AUTODESK INVENTOR PART (.ipt)
format: ipt  version: 2018 (Build 220112000, 112)  size: 104,690,176 bytes
history: native  units: in
note: dims shown in document units (in); Inventor stores cm internally (conversion verified against a paired STEP export)
features: other x1942, extrude x30
ambient origin geometry x8: Origin, YZ Plane, XZ Plane, XY Plane, X Axis, Y Axis, Z Axis, Center Point
bodies: Solid1 (feature_tree), Solid2 (feature_tree), Solid3 (feature_tree), Solid4 (feature_tree), Solid5 (feature_tree), Solid6 (feature_tree), Solid7 (feature_tree), Solid8 (feature_tree), Solid9 (feature_tree), Solid10 (feature_tree), Solid11 (feature_tree), Solid12 (feature_tree), Solid13 (feature_tree), Solid14 (feature_tree), Solid15 (feature_tree), Solid16 (feature_tree), Solid17 (feature_tree), Solid18 (feature_tree), Solid19 (feature_tree), Solid20 (feature_tree), Solid21 (feature_tree), Solid22 (feature_tree), Solid23 (feature_tree), Solid24 (feature_tree), Solid25 (feature_tree), Solid26 (feature_tree), Solid27 (feature_tree), Solid28 (feature_tree), Solid29 (feature_tree), Solid30 (feature_tree), Solid31 (feature_tree), Solid32 (feature_tree), Solid33 (feature_tree), Solid34 (feature_tree), Solid35 (feature_tree), Solid36 (feature_tree), Solid37 (feature_tree), Solid38 (feature_tree), Solid39 (feature_tree), Solid40 (feature_tree), Solid41 (feature_tree), Solid42 (feature_tree), Solid43 (feature_tree), Solid44 (feature_tree), Solid45 (feature_tree), Solid46 (feature_tree), Solid47 (feature_tree), Solid48 (feature_tree), Solid49 (feature_tree), Solid50 (feature_tree), Solid51 (feature_tree), Solid52 (feature_tree), Solid53 (feature_tree), Solid54 (feature_tree), Solid55 (feature_tree), Solid56 (feature_tree), Solid57 (feature_tree), Solid58 (feature_tree), Solid59 (feature_tree), Solid60 (feature_tree), Solid61 (feature_tree), Solid62 (feature_tree), Solid63 (feature_tree), Solid64 (feature_tree), Solid65 (feature_tree), Solid66 (feature_tree), Solid67 (feature_tree), Solid68 (feature_tree), Solid69 (feature_tree), Solid70 (feature_tree), Solid71 (feature_tree), Solid72 (feature_tree), Solid73 (feature_tree), Solid74 (feature_tree), Solid75 (feature_tree), Solid76 (feature_tree), Solid77 (feature_tree), Solid78 (feature_tree), Solid79 (feature_tree), Solid80 (feature_tree), Solid81 (feature_tree), Solid82 (feature_tree), Solid83 (feature_tree), Solid84 (feature_tree), Solid85 (feature_tree), Solid86 (feature_tree), Solid87 (feature_tree), Solid88 (feature_tree), Solid89 (feature_tree), Solid90 (feature_tree), Solid91 (feature_tree), Solid92 (feature_tree), Solid93 (feature_tree), Solid94 (feature_tree), Solid95 (feature_tree), Solid96 (feature_tree), Solid97 (feature_tree), Solid98 (feature_tree), Solid99 (feature_tree), Solid100 (feature_tree), Solid101 (feature_tree), Solid102 (feature_tree), Solid103 (feature_tree), Solid104 (feature_tree), Solid105 (feature_tree), Solid106 (feature_tree), Solid107 (feature_tree), Solid108 (feature_tree), Solid109 (feature_tree), Solid110 (feature_tree), Solid111 (feature_tree), Solid112 (feature_tree), Solid113 (feature_tree), Solid114 (feature_tree), Solid115 (feature_tree), Solid116 (feature_tree), Solid117 (feature_tree), Solid118 (feature_tree), Solid119 (feature_tree), Solid120 (feature_tree), Solid121 (feature_tree), Solid122 (feature_tree), Solid123 (feature_tree), Solid124 (feature_tree), Solid125 (feature_tree), Solid126 (feature_tree), Solid127 (feature_tree), Solid128 (feature_tree), Solid129 (feature_tree), Solid130 (feature_tree), Solid131 (feature_tree), Solid132 (feature_tree), Solid133 (feature_tree), Solid134 (feature_tree), Solid135 (feature_tree), Solid136 (feature_tree), Solid137 (feature_tree), Solid138 (feature_tree), Solid139 (feature_tree), Solid140 (feature_tree), Solid141 (feature_tree), Solid142 (feature_tree), Solid143 (feature_tree), Solid144 (feature_tree), Solid145 (feature_tree), Solid146 (feature_tree), Solid147 (feature_tree), Solid148 (feature_tree), Solid149 (feature_tree), Solid150 (feature_tree), Solid151 (feature_tree), Solid152 (feature_tree), Solid153 (feature_tree), Solid154 (feature_tree), Solid155 (feature_tree), Solid156 (feature_tree), Solid157 (feature_tree), Solid158 (feature_tree), Solid159 (feature_tree), Solid160 (feature_tree), Solid161 (feature_tree), Solid162 (feature_tree), Solid163 (feature_tree), Solid164 (feature_tree), Solid165 (feature_tree), Solid166 (feature_tree), Solid167 (feature_tree), Solid168 (feature_tree), Solid169 (feature_tree), Solid170 (feature_tree), Solid171 (feature_tree), Solid172 (feature_tree), Solid173 (feature_tree), Solid174 (feature_tree), Solid175 (feature_tree), Solid176 (feature_tree), Solid177 (feature_tree), Solid178 (feature_tree), Solid179 (feature_tree), Solid180 (feature_tree), Solid181 (feature_tree), Solid182 (feature_tree), Solid183 (feature_tree), Solid184 (feature_tree), Solid185 (feature_tree), Solid186 (feature_tree), Solid187 (feature_tree), Solid188 (feature_tree), Solid189 (feature_tree), Solid190 (feature_tree), Solid191 (feature_tree), Solid192 (feature_tree), Solid193 (feature_tree), Solid194 (feature_tree), Solid195 (feature_tree), Solid196 (feature_tree), Solid197 (feature_tree), Solid198 (feature_tree), Solid199 (feature_tree), Solid200 (feature_tree), Solid201 (feature_tree), Solid202 (feature_tree), Solid203 (feature_tree), Solid204 (feature_tree), Solid205 (feature_tree), Solid206 (feature_tree), Solid207 (feature_tree), Solid208 (feature_tree), Solid209 (feature_tree), Solid210 (feature_tree), Solid211 (feature_tree), Solid212 (feature_tree), Solid213 (feature_tree), Solid214 (feature_tree), Solid215 (feature_tree), Solid216 (feature_tree), Solid217 (feature_tree), Solid218 (feature_tree), Solid219 (feature_tree), Solid220 (feature_tree), Solid221 (feature_tree), Solid222 (feature_tree), Solid223 (feature_tree), Solid224 (feature_tree), Solid225 (feature_tree), Solid226 (feature_tree), Solid227 (feature_tree), Solid228 (feature_tree), Solid229 (feature_tree), Solid230 (feature_tree), Solid231 (feature_tree), Solid232 (feature_tree), Solid233 (feature_tree), Solid234 (feature_tree), Solid235 (feature_tree), Solid236 (feature_tree), Solid237 (feature_tree), Solid238 (feature_tree), Solid239 (feature_tree), Solid240 (feature_tree), Solid241 (feature_tree), Solid242 (feature_tree), Solid243 (feature_tree), Solid244 (feature_tree), Solid245 (feature_tree), Solid246 (feature_tree), Solid247 (feature_tree), Solid248 (feature_tree), Solid249 (feature_tree), Solid250 (feature_tree), Solid251 (feature_tree), Solid252 (feature_tree), Solid253 (feature_tree), Solid254 (feature_tree), Solid255 (feature_tree), Solid256 (feature_tree), Solid257 (feature_tree), Solid258 (feature_tree), Solid259 (feature_tree), Solid260 (feature_tree), Solid261 (feature_tree), Solid262 (feature_tree), Solid263 (feature_tree), Solid264 (feature_tree), Solid265 (feature_tree), Solid266 (feature_tree), Solid267 (feature_tree), Solid268 (feature_tree), Solid269 (feature_tree), Solid270 (feature_tree), Solid271 (feature_tree), Solid272 (feature_tree), Solid273 (feature_tree), Solid274 (feature_tree), Solid275 (feature_tree), Solid276 (feature_tree), Solid277 (feature_tree), Solid278 (feature_tree), Solid279 (feature_tree), Solid280 (feature_tree), Solid281 (feature_tree), Solid282 (feature_tree), Solid283 (feature_tree), Solid284 (feature_tree), Solid285 (feature_tree), Solid286 (feature_tree), Solid287 (feature_tree), Solid288 (feature_tree), Solid289 (feature_tree), Solid290 (feature_tree), Solid291 (feature_tree), Solid292 (feature_tree), Solid293 (feature_tree), Solid294 (feature_tree), Solid295 (feature_tree), Solid296 (feature_tree), Solid297 (feature_tree), Solid298 (feature_tree), Solid299 (feature_tree), Solid300 (feature_tree), Solid301 (feature_tree), Solid302 (feature_tree), Solid303 (feature_tree), Solid304 (feature_tree), Solid305 (feature_tree), Solid306 (feature_tree), Solid307 (feature_tree), Solid308 (feature_tree), Solid309 (feature_tree), Solid310 (feature_tree), Solid311 (feature_tree), Solid312 (feature_tree), Solid313 (feature_tree), Solid314 (feature_tree), Solid315 (feature_tree), Solid316 (feature_tree), Solid317 (feature_tree), Solid318 (feature_tree), Solid319 (feature_tree), Solid320 (feature_tree), Solid321 (feature_tree), Solid322 (feature_tree), Solid323 (feature_tree), Solid324 (feature_tree), Solid325 (feature_tree), Solid326 (feature_tree), Solid327 (feature_tree), Solid328 (feature_tree), Solid329 (feature_tree), Solid330 (feature_tree), Solid331 (feature_tree), Solid332 (feature_tree), Solid333 (feature_tree), Solid334 (feature_tree), Solid335 (feature_tree), Solid336 (feature_tree), Solid337 (feature_tree), Solid338 (feature_tree), Solid339 (feature_tree), Solid340 (feature_tree), Solid341 (feature_tree), Solid342 (feature_tree), Solid343 (feature_tree), Solid344 (feature_tree), Solid345 (feature_tree), Solid346 (feature_tree), Solid347 (feature_tree), Solid348 (feature_tree), Solid349 (feature_tree), Solid350 (feature_tree), Solid351 (feature_tree), Solid352 (feature_tree), Solid353 (feature_tree), Solid354 (feature_tree), Solid355 (feature_tree), Solid356 (feature_tree), Solid357 (feature_tree), Solid358 (feature_tree), Solid359 (feature_tree), Solid360 (feature_tree), Solid361 (feature_tree), Solid362 (feature_tree), Solid363 (feature_tree), Solid364 (feature_tree), Solid365 (feature_tree), Solid366 (feature_tree), Solid367 (feature_tree), Solid368 (feature_tree), Solid369 (feature_tree), Solid370 (feature_tree), Solid371 (feature_tree), Solid372 (feature_tree), Solid373 (feature_tree), Solid374 (feature_tree), Solid375 (feature_tree), Solid376 (feature_tree), Solid377 (feature_tree), Solid378 (feature_tree), Solid379 (feature_tree), Solid380 (feature_tree), Solid381 (feature_tree), Solid382 (feature_tree), Solid383 (feature_tree), Solid384 (feature_tree), Solid385 (feature_tree), Solid386 (feature_tree), Solid387 (feature_tree), Solid388 (feature_tree), Solid389 (feature_tree), Solid390 (feature_tree), Solid391 (feature_tree), Solid392 (feature_tree), Solid393 (feature_tree), Solid394 (feature_tree), Solid395 (feature_tree), Solid396 (feature_tree), Solid397 (feature_tree), Solid398 (feature_tree), Solid399 (feature_tree), Solid400 (feature_tree), Solid401 (feature_tree), Solid402 (feature_tree), Solid403 (feature_tree), Solid404 (feature_tree), Solid405 (feature_tree), Solid406 (feature_tree), Solid407 (feature_tree), Solid408 (feature_tree), Solid409 (feature_tree), Solid410 (feature_tree), Solid411 (feature_tree), Solid412 (feature_tree), Solid413 (feature_tree), Solid414 (feature_tree), Solid415 (feature_tree), Solid416 (feature_tree), Solid417 (feature_tree), Solid418 (feature_tree), Solid419 (feature_tree), Solid420 (feature_tree), Solid421 (feature_tree), Solid422 (feature_tree), Solid423 (feature_tree), Solid424 (feature_tree), Solid425 (feature_tree), Solid426 (feature_tree), Solid427 (feature_tree), Solid428 (feature_tree), Solid429 (feature_tree), Solid430 (feature_tree), Solid431 (feature_tree), Solid432 (feature_tree), Solid433 (feature_tree), Solid434 (feature_tree), Solid435 (feature_tree), Solid436 (feature_tree), Solid437 (feature_tree), Solid438 (feature_tree), Solid439 (feature_tree), Solid440 (feature_tree), Solid441 (feature_tree), Solid442 (feature_tree), Solid443 (feature_tree), Solid444 (feature_tree), Solid445 (feature_tree), Solid446 (feature_tree), Solid447 (feature_tree), Solid448 (feature_tree), Solid449 (feature_tree), Solid450 (feature_tree), Solid451 (feature_tree), Solid452 (feature_tree), Solid453 (feature_tree), Solid454 (feature_tree), Solid455 (feature_tree), Solid456 (feature_tree), Solid457 (feature_tree), Solid458 (feature_tree), Solid459 (feature_tree), Solid460 (feature_tree), Solid461 (feature_tree), Solid462 (feature_tree), Solid463 (feature_tree), Solid464 (feature_tree), Solid465 (feature_tree), Solid466 (feature_tree), Solid467 (feature_tree), Solid468 (feature_tree), Solid469 (feature_tree), Solid470 (feature_tree), Solid471 (feature_tree), Solid472 (feature_tree), Solid473 (feature_tree), Solid474 (feature_tree), Solid475 (feature_tree), Solid476 (feature_tree), Solid477 (feature_tree), Solid478 (feature_tree), Solid479 (feature_tree), Solid480 (feature_tree), Solid481 (feature_tree), Solid482 (feature_tree), Solid483 (feature_tree), Solid484 (feature_tree), Solid485 (feature_tree), Solid486 (feature_tree), Solid487 (feature_tree), Solid488 (feature_tree), Solid489 (feature_tree), Solid490 (feature_tree), Solid491 (feature_tree), Solid492 (feature_tree), Solid493 (feature_tree), Solid494 (feature_tree), Solid495 (feature_tree), Solid496 (feature_tree), Solid497 (feature_tree), Solid498 (feature_tree), Solid499 (feature_tree), Solid500 (feature_tree), Solid501 (feature_tree), Solid502 (feature_tree), Solid503 (feature_tree), Solid504 (feature_tree), Solid505 (feature_tree), Solid506 (feature_tree), Solid507 (feature_tree), Solid508 (feature_tree), Solid509 (feature_tree), Solid510 (feature_tree), Solid511 (feature_tree), Solid512 (feature_tree), Solid513 (feature_tree), Solid514 (feature_tree), Solid515 (feature_tree), Solid516 (feature_tree), Solid517 (feature_tree), Solid518 (feature_tree), Solid519 (feature_tree), Solid520 (feature_tree), Solid521 (feature_tree), Solid522 (feature_tree), Solid523 (feature_tree), Solid524 (feature_tree), Solid525 (feature_tree), Solid526 (feature_tree), Solid527 (feature_tree), Solid528 (feature_tree), Solid529 (feature_tree), Solid530 (feature_tree), Solid531 (feature_tree), Solid532 (feature_tree), Solid533 (feature_tree), Solid534 (feature_tree), Solid535 (feature_tree), Solid536 (feature_tree), Solid537 (feature_tree), Solid538 (feature_tree), Solid539 (feature_tree), Solid540 (feature_tree), Solid541 (feature_tree), Solid542 (feature_tree), Solid543 (feature_tree), Solid544 (feature_tree), Solid545 (feature_tree), Solid546 (feature_tree), Solid547 (feature_tree), Solid548 (feature_tree), Solid549 (feature_tree), Solid550 (feature_tree), Solid551 (feature_tree), Solid552 (feature_tree), Solid553 (feature_tree), Solid554 (feature_tree), Solid555 (feature_tree), Solid556 (feature_tree), Solid557 (feature_tree), Solid558 (feature_tree), Solid559 (feature_tree), Solid560 (feature_tree), Solid561 (feature_tree), Solid562 (feature_tree), Solid563 (feature_tree), Solid564 (feature_tree), Solid565 (feature_tree), Solid566 (feature_tree), Solid567 (feature_tree), Solid568 (feature_tree), Solid569 (feature_tree), Solid570 (feature_tree), Solid571 (feature_tree), Solid572 (feature_tree), Solid573 (feature_tree), Solid574 (feature_tree), Solid575 (feature_tree), Solid576 (feature_tree), Solid577 (feature_tree), Solid578 (feature_tree), Solid579 (feature_tree), Solid580 (feature_tree), Solid581 (feature_tree), Solid582 (feature_tree), Solid583 (feature_tree), Solid584 (feature_tree), Solid585 (feature_tree), Solid586 (feature_tree), Solid587 (feature_tree), Solid588 (feature_tree), Solid589 (feature_tree), Solid590 (feature_tree), Solid591 (feature_tree), Solid592 (feature_tree), Solid593 (feature_tree), Solid594 (feature_tree), Solid595 (feature_tree), Solid596 (feature_tree), Solid597 (feature_tree), Solid598 (feature_tree), Solid599 (feature_tree), Solid600 (feature_tree), Solid601 (feature_tree), Solid602 (feature_tree), Solid603 (feature_tree), Solid604 (feature_tree), Solid605 (feature_tree), Solid606 (feature_tree), Solid607 (feature_tree), Solid608 (feature_tree), Solid609 (feature_tree), Solid610 (feature_tree), Solid611 (feature_tree), Solid612 (feature_tree), Solid613 (feature_tree), Solid614 (feature_tree), Solid615 (feature_tree), Solid616 (feature_tree), Solid617 (feature_tree), Solid618 (feature_tree), Solid619 (feature_tree), Solid620 (feature_tree), Solid621 (feature_tree), Solid622 (feature_tree), Solid623 (feature_tree), Solid624 (feature_tree), Solid625 (feature_tree), Solid626 (feature_tree), Solid627 (feature_tree), Solid628 (feature_tree), Solid629 (feature_tree), Solid630 (feature_tree), Solid631 (feature_tree), Solid632 (feature_tree), Solid633 (feature_tree), Solid634 (feature_tree), Solid635 (feature_tree), Solid636 (feature_tree), Solid637 (feature_tree), Solid638 (feature_tree), Solid639 (feature_tree), Solid640 (feature_tree), Solid641 (feature_tree), Solid642 (feature_tree), Solid643 (feature_tree), Solid644 (feature_tree), Solid645 (feature_tree), Solid646 (feature_tree), Solid647 (feature_tree), Solid648 (feature_tree), Solid649 (feature_tree), Solid650 (feature_tree), Solid651 (feature_tree), Solid652 (feature_tree), Solid653 (feature_tree), Solid654 (feature_tree), Solid655 (feature_tree), Solid656 (feature_tree), Solid657 (feature_tree), Solid658 (feature_tree), Solid659 (feature_tree), Solid660 (feature_tree), Solid661 (feature_tree), Solid662 (feature_tree), Solid663 (feature_tree), Solid664 (feature_tree), Solid665 (feature_tree), Solid666 (feature_tree), Solid667 (feature_tree), Solid668 (feature_tree), Solid669 (feature_tree), Solid670 (feature_tree), Solid671 (feature_tree), Solid672 (feature_tree), Solid673 (feature_tree), Solid674 (feature_tree), Solid675 (feature_tree), Solid676 (feature_tree), Solid677 (feature_tree), Solid678 (feature_tree), Solid679 (feature_tree), Solid680 (feature_tree), Solid681 (feature_tree), Solid682 (feature_tree), Solid683 (feature_tree), Solid684 (feature_tree), Solid685 (feature_tree), Solid686 (feature_tree), Solid687 (feature_tree), Solid688 (feature_tree), Solid689 (feature_tree), Solid690 (feature_tree), Solid691 (feature_tree), Solid692 (feature_tree), Solid693 (feature_tree), Solid694 (feature_tree), Solid695 (feature_tree), Solid696 (feature_tree), Solid697 (feature_tree), Solid698 (feature_tree), Solid699 (feature_tree), Solid700 (feature_tree), Solid701 (feature_tree), Solid702 (feature_tree), Solid703 (feature_tree), Solid704 (feature_tree), Solid705 (feature_tree), Solid706 (feature_tree), Solid707 (feature_tree), Solid708 (feature_tree), Solid709 (feature_tree), Solid710 (feature_tree), Solid711 (feature_tree), Solid712 (feature_tree), Solid713 (feature_tree), Solid714 (feature_tree), Solid715 (feature_tree), Solid716 (feature_tree), Solid717 (feature_tree), Solid718 (feature_tree), Solid719 (feature_tree), Solid720 (feature_tree), Solid721 (feature_tree), Solid722 (feature_tree), Solid723 (feature_tree), Solid724 (feature_tree), Solid725 (feature_tree), Solid726 (feature_tree), Solid727 (feature_tree), Solid728 (feature_tree), Solid729 (feature_tree), Solid730 (feature_tree), Solid731 (feature_tree), Solid732 (feature_tree), Solid733 (feature_tree), Solid734 (feature_tree), Solid735 (feature_tree), Solid736 (feature_tree), Solid737 (feature_tree), Solid738 (feature_tree), Solid739 (feature_tree), Solid740 (feature_tree), Solid741 (feature_tree), Solid742 (feature_tree), Solid743 (feature_tree), Solid744 (feature_tree), Solid745 (feature_tree), Solid746 (feature_tree), Solid747 (feature_tree), Solid748 (feature_tree), Solid749 (feature_tree), Solid750 (feature_tree), Solid751 (feature_tree), Solid752 (feature_tree), Solid753 (feature_tree), Solid754 (feature_tree), Solid755 (feature_tree), Solid756 (feature_tree), Solid757 (feature_tree), Solid758 (feature_tree), Solid759 (feature_tree), Solid760 (feature_tree), Solid761 (feature_tree), Solid762 (feature_tree), Solid763 (feature_tree), Solid764 (feature_tree), Solid765 (feature_tree), Solid766 (feature_tree), Solid767 (feature_tree), Solid768 (feature_tree), Solid769 (feature_tree), Solid770 (feature_tree), Solid771 (feature_tree), Solid772 (feature_tree), Solid773 (feature_tree), Solid774 (feature_tree), Solid775 (feature_tree), Solid776 (feature_tree), Solid777 (feature_tree), Solid778 (feature_tree), Solid779 (feature_tree), Solid780 (feature_tree), Solid781 (feature_tree), Solid782 (feature_tree), Solid783 (feature_tree), Solid784 (feature_tree), Solid785 (feature_tree), Solid786 (feature_tree), Solid787 (feature_tree), Solid788 (feature_tree), Solid789 (feature_tree), Solid790 (feature_tree), Solid791 (feature_tree), Solid792 (feature_tree), Solid793 (feature_tree), Solid794 (feature_tree), Solid795 (feature_tree), Solid796 (feature_tree), Solid797 (feature_tree), Solid798 (feature_tree), Solid799 (feature_tree), Solid800 (feature_tree), Solid801 (feature_tree), Solid802 (feature_tree), Solid803 (feature_tree), Solid804 (feature_tree), Solid805 (feature_tree), Solid806 (feature_tree), Solid807 (feature_tree), Solid808 (feature_tree), Solid809 (feature_tree), Solid810 (feature_tree), Solid811 (feature_tree), Solid812 (feature_tree), Solid813 (feature_tree), Solid814 (feature_tree), Solid815 (feature_tree), Solid816 (feature_tree), Solid817 (feature_tree), Solid818 (feature_tree), Solid819 (feature_tree), Solid820 (feature_tree), Solid821 (feature_tree), Solid822 (feature_tree), Solid823 (feature_tree), Solid824 (feature_tree), Solid825 (feature_tree), Solid826 (feature_tree), Solid827 (feature_tree), Solid828 (feature_tree), Solid829 (feature_tree), Solid830 (feature_tree), Solid831 (feature_tree), Solid832 (feature_tree), Solid833 (feature_tree), Solid834 (feature_tree), Solid835 (feature_tree), Solid836 (feature_tree), Solid837 (feature_tree), Solid838 (feature_tree), Solid839 (feature_tree), Solid840 (feature_tree), Solid841 (feature_tree), Solid842 (feature_tree), Solid843 (feature_tree), Solid844 (feature_tree), Solid845 (feature_tree), Solid846 (feature_tree), Solid847 (feature_tree), Solid848 (feature_tree), Solid849 (feature_tree), Solid850 (feature_tree), Solid851 (feature_tree), Solid852 (feature_tree), Solid853 (feature_tree), Solid854 (feature_tree), Solid855 (feature_tree), Solid856 (feature_tree), Solid857 (feature_tree), Solid858 (feature_tree), Solid859 (feature_tree), Solid860 (feature_tree), Solid861 (feature_tree), Solid862 (feature_tree), Solid863 (feature_tree), Solid864 (feature_tree), Solid865 (feature_tree), Solid866 (feature_tree), Solid867 (feature_tree), Solid868 (feature_tree), Solid869 (feature_tree), Solid870 (feature_tree), Solid871 (feature_tree), Solid872 (feature_tree), Solid873 (feature_tree), Solid874 (feature_tree), Solid875 (feature_tree), Solid876 (feature_tree), Solid877 (feature_tree), Solid878 (feature_tree), Solid879 (feature_tree), Solid880 (feature_tree), Solid881 (feature_tree), Solid882 (feature_tree), Solid883 (feature_tree), Solid884 (feature_tree), Solid885 (feature_tree), Solid886 (feature_tree), Solid887 (feature_tree), Solid888 (feature_tree), Solid889 (feature_tree), Solid890 (feature_tree), Solid891 (feature_tree), Solid892 (feature_tree), Solid893 (feature_tree), Solid894 (feature_tree), Solid895 (feature_tree), Solid896 (feature_tree), Solid897 (feature_tree), Solid898 (feature_tree), Solid899 (feature_tree), Solid900 (feature_tree), Solid901 (feature_tree), Solid902 (feature_tree), Solid903 (feature_tree), Solid904 (feature_tree), Solid905 (feature_tree), Solid906 (feature_tree), Solid907 (feature_tree), Solid908 (feature_tree), Solid909 (feature_tree), Solid910 (feature_tree), Solid911 (feature_tree), Solid912 (feature_tree), Solid913 (feature_tree), Solid914 (feature_tree), Solid915 (feature_tree), Solid916 (feature_tree), Solid917 (feature_tree), Solid918 (feature_tree), Solid919 (feature_tree), Solid920 (feature_tree), Solid921 (feature_tree), Solid922 (feature_tree), Solid923 (feature_tree), Solid924 (feature_tree), Solid925 (feature_tree), Solid926 (feature_tree), Solid927 (feature_tree), Solid928 (feature_tree), Solid929 (feature_tree), Solid930 (feature_tree), Solid931 (feature_tree), Solid932 (feature_tree), Solid933 (feature_tree), Solid934 (feature_tree), Solid935 (feature_tree), Solid936 (feature_tree), Solid937 (feature_tree), Solid938 (feature_tree), Solid939 (feature_tree), Solid940 (feature_tree), Solid941 (feature_tree), Solid942 (feature_tree), Solid943 (feature_tree), Solid944 (feature_tree), Solid945 (feature_tree), Solid946 (feature_tree), Solid947 (feature_tree), Solid948 (feature_tree), Solid949 (feature_tree), Solid950 (feature_tree), Solid951 (feature_tree), Solid952 (feature_tree), Solid953 (feature_tree), Solid954 (feature_tree), Solid955 (feature_tree), Solid956 (feature_tree), Solid957 (feature_tree), Solid958 (feature_tree), Solid959 (feature_tree), Solid960 (feature_tree), Solid961 (feature_tree), Solid962 (feature_tree), Solid963 (feature_tree), Solid964 (feature_tree), Solid965 (feature_tree), Solid966 (feature_tree), Solid967 (feature_tree), Solid968 (feature_tree), Solid969 (feature_tree), Solid970 (feature_tree), Solid971 (feature_tree), Solid972 (feature_tree), Solid973 (feature_tree), Solid974 (feature_tree), Solid975 (feature_tree), Solid976 (feature_tree), Solid977 (feature_tree), Solid978 (feature_tree), Solid979 (feature_tree), Solid980 (feature_tree), Solid981 (feature_tree), Solid982 (feature_tree), Solid983 (feature_tree), Solid984 (feature_tree), Solid985 (feature_tree), Solid986 (feature_tree), Solid987 (feature_tree), Solid988 (feature_tree), Solid989 (feature_tree), Solid990 (feature_tree), Solid991 (feature_tree), Solid992 (feature_tree), Solid993 (feature_tree), Solid994 (feature_tree), Solid995 (feature_tree), Solid996 (feature_tree), Solid997 (feature_tree), Solid998 (feature_tree), Solid999 (feature_tree), Solid1000 (feature_tree), Solid1001 (feature_tree), Solid1002 (feature_tree), Solid1003 (feature_tree), Solid1004 (feature_tree), Solid1005 (feature_tree), Solid1006 (feature_tree), Solid1007 (feature_tree), Solid1008 (feature_tree), Solid1009 (feature_tree), Solid1010 (feature_tree), Solid1011 (feature_tree), Solid1012 (feature_tree), Solid1013 (feature_tree), Solid1014 (feature_tree), Solid1015 (feature_tree), Solid1016 (feature_tree), Solid1017 (feature_tree), Solid1018 (feature_tree), Solid1019 (feature_tree), Solid1020 (feature_tree), Solid1021 (feature_tree), Solid1022 (feature_tree), Solid1023 (feature_tree), Solid1024 (feature_tree), Solid1025 (feature_tree), Solid1026 (feature_tree), Solid1027 (feature_tree), Solid1028 (feature_tree), Solid1029 (feature_tree), Solid1030 (feature_tree), Solid1031 (feature_tree), Solid1032 (feature_tree), Solid1033 (feature_tree), Solid1034 (feature_tree), Solid1035 (feature_tree), Solid1036 (feature_tree), Solid1037 (feature_tree), Solid1038 (feature_tree), Solid1039 (feature_tree), Solid1040 (feature_tree), Solid1041 (feature_tree), Solid1042 (feature_tree), Solid1043 (feature_tree), Solid1044 (feature_tree), Solid1045 (feature_tree), Solid1046 (feature_tree), Solid1047 (feature_tree), Solid1048 (feature_tree), Solid1049 (feature_tree), Solid1050 (feature_tree), Solid1051 (feature_tree), Solid1052 (feature_tree), Solid1053 (feature_tree), Solid1054 (feature_tree), Solid1055 (feature_tree), Solid1056 (feature_tree), Solid1057 (feature_tree), Solid1058 (feature_tree), Solid1059 (feature_tree), Solid1060 (feature_tree), Solid1061 (feature_tree), Solid1062 (feature_tree), Solid1063 (feature_tree), Solid1064 (feature_tree), Solid1065 (feature_tree), Solid1066 (feature_tree), Solid1067 (feature_tree), Solid1068 (feature_tree), Solid1069 (feature_tree), Solid1070 (feature_tree), Solid1071 (feature_tree), Solid1072 (feature_tree), Solid1073 (feature_tree), Solid1074 (feature_tree), Solid1075 (feature_tree), Solid1076 (feature_tree), Solid1077 (feature_tree), Solid1078 (feature_tree), Solid1079 (feature_tree), Solid1080 (feature_tree), Solid1081 (feature_tree), Solid1082 (feature_tree), Solid1083 (feature_tree), Solid1084 (feature_tree), Solid1085 (feature_tree), Solid1086 (feature_tree), Solid1087 (feature_tree), Solid1088 (feature_tree), Solid1089 (feature_tree), Solid1090 (feature_tree), Solid1091 (feature_tree), Solid1092 (feature_tree), Solid1093 (feature_tree), Solid1094 (feature_tree), Solid1095 (feature_tree), Solid1096 (feature_tree), Solid1097 (feature_tree), Solid1098 (feature_tree), Solid1099 (feature_tree), Solid1100 (feature_tree), Solid1101 (feature_tree), Solid1102 (feature_tree), Solid1103 (feature_tree), Solid1104 (feature_tree), Solid1105 (feature_tree), Solid1106 (feature_tree), Solid1107 (feature_tree), Solid1108 (feature_tree), Solid1109 (feature_tree), Solid1110 (feature_tree), Solid1111 (feature_tree), Solid1112 (feature_tree), Solid1113 (feature_tree), Solid1114 (feature_tree), Solid1115 (feature_tree), Solid1116 (feature_tree), Solid1117 (feature_tree), Solid1118 (feature_tree), Solid1119 (feature_tree), Solid1120 (feature_tree), Solid1121 (feature_tree), Solid1122 (feature_tree), Solid1123 (feature_tree), Solid1124 (feature_tree), Solid1125 (feature_tree), Solid1126 (feature_tree), Solid1127 (feature_tree), Solid1128 (feature_tree), Solid1129 (feature_tree), Solid1130 (feature_tree), Solid1131 (feature_tree), Solid1132 (feature_tree), Solid1133 (feature_tree), Solid1134 (feature_tree), Solid1135 (feature_tree), Solid1136 (feature_tree), Solid1137 (feature_tree), Solid1138 (feature_tree), Solid1139 (feature_tree), Solid1140 (feature_tree), Solid1141 (feature_tree), Solid1142 (feature_tree), Solid1143 (feature_tree), Solid1144 (feature_tree), Solid1145 (feature_tree), Solid1146 (feature_tree), Solid1147 (feature_tree), Solid1148 (feature_tree), Solid1149 (feature_tree), Solid1150 (feature_tree), Solid1151 (feature_tree), Solid1152 (feature_tree), Solid1153 (feature_tree), Solid1154 (feature_tree), Solid1155 (feature_tree), Solid1156 (feature_tree), Solid1157 (feature_tree), Solid1158 (feature_tree), Solid1159 (feature_tree), Solid1160 (feature_tree), Solid1161 (feature_tree), Solid1162 (feature_tree), Solid1163 (feature_tree), Solid1164 (feature_tree), Solid1165 (feature_tree), Solid1166 (feature_tree), Solid1167 (feature_tree), Solid1168 (feature_tree), Solid1169 (feature_tree), Solid1170 (feature_tree), Solid1171 (feature_tree), Solid1172 (feature_tree), Solid1173 (feature_tree), Solid1174 (feature_tree), Solid1175 (feature_tree), Solid1176 (feature_tree), Solid1177 (feature_tree), Solid1178 (feature_tree), Solid1179 (feature_tree), Solid1180 (feature_tree), Solid1181 (feature_tree), Solid1182 (feature_tree), Solid1183 (feature_tree), Solid1184 (feature_tree), Solid1185 (feature_tree), Solid1186 (feature_tree), Solid1187 (feature_tree), Solid1188 (feature_tree), Solid1189 (feature_tree), Solid1190 (feature_tree), Solid1191 (feature_tree), Solid1192 (feature_tree), Solid1193 (feature_tree), Solid1194 (feature_tree), Solid1195 (feature_tree), Solid1196 (feature_tree), Solid1197 (feature_tree), Solid1198 (feature_tree), Solid1199 (feature_tree), Solid1200 (feature_tree), Solid1201 (feature_tree), Solid1202 (feature_tree), Solid1203 (feature_tree), Solid1204 (feature_tree), Solid1205 (feature_tree), Solid1206 (feature_tree), Solid1207 (feature_tree), Solid1208 (feature_tree), Solid1209 (feature_tree), Solid1210 (feature_tree), Solid1211 (feature_tree), Solid1212 (feature_tree), Solid1213 (feature_tree), Solid1214 (feature_tree), Solid1215 (feature_tree), Solid1216 (feature_tree), Solid1217 (feature_tree), Solid1218 (feature_tree), Solid1219 (feature_tree), Solid1220 (feature_tree), Solid1221 (feature_tree), Solid1222 (feature_tree), Solid1223 (feature_tree), Solid1224 (feature_tree), Solid1225 (feature_tree), Solid1226 (feature_tree), Solid1227 (feature_tree), Solid1228 (feature_tree), Solid1229 (feature_tree), Solid1230 (feature_tree), Solid1231 (feature_tree), Solid1232 (feature_tree), Solid1233 (feature_tree), Solid1234 (feature_tree), Solid1235 (feature_tree), Solid1236 (feature_tree), Solid1237 (feature_tree), Solid1238 (feature_tree), Solid1239 (feature_tree), Solid1240 (feature_tree), Solid1241 (feature_tree), Solid1242 (feature_tree), Solid1243 (feature_tree), Solid1244 (feature_tree), Solid1245 (feature_tree), Solid1246 (feature_tree), Solid1247 (feature_tree), Solid1248 (feature_tree), Solid1249 (feature_tree), Solid1250 (feature_tree), Solid1251 (feature_tree), Solid1252 (feature_tree), Solid1253 (feature_tree), Solid1254 (feature_tree), Solid1255 (feature_tree), Solid1256 (feature_tree), Solid1257 (feature_tree), Solid1258 (feature_tree), Solid1259 (feature_tree), Solid1260 (feature_tree), Solid1261 (feature_tree), Solid1262 (feature_tree), Solid1263 (feature_tree), Solid1264 (feature_tree), Solid1265 (feature_tree), Solid1266 (feature_tree), Solid1267 (feature_tree), Solid1268 (feature_tree), Solid1269 (feature_tree), Solid1270 (feature_tree), Solid1271 (feature_tree), Solid1272 (feature_tree), Solid1273 (feature_tree), Solid1274 (feature_tree), Solid1275 (feature_tree), Solid1276 (feature_tree), Solid1277 (feature_tree), Solid1278 (feature_tree), Solid1279 (feature_tree), Solid1280 (feature_tree), Solid1281 (feature_tree), Solid1282 (feature_tree), Solid1283 (feature_tree), Solid1284 (feature_tree), Solid1285 (feature_tree), Solid1286 (feature_tree), Solid1287 (feature_tree), Solid1288 (feature_tree), Solid1289 (feature_tree), Solid1290 (feature_tree), Solid1291 (feature_tree), Solid1292 (feature_tree), Solid1293 (feature_tree), Solid1294 (feature_tree), Solid1295 (feature_tree), Solid1296 (feature_tree), Solid1297 (feature_tree), Solid1298 (feature_tree), Solid1299 (feature_tree), Solid1300 (feature_tree), Solid1301 (feature_tree), Solid1302 (feature_tree), Solid1303 (feature_tree), Solid1304 (feature_tree), Solid1305 (feature_tree), Solid1306 (feature_tree), Solid1307 (feature_tree), Solid1308 (feature_tree), Solid1309 (feature_tree), Solid1310 (feature_tree), Solid1311 (feature_tree), Solid1312 (feature_tree), Solid1313 (feature_tree), Solid1314 (feature_tree), Solid1315 (feature_tree), Solid1316 (feature_tree), Solid1317 (feature_tree), Solid1318 (feature_tree), Solid1319 (feature_tree), Solid1320 (feature_tree), Solid1321 (feature_tree), Solid1322 (feature_tree), Solid1323 (feature_tree), Solid1324 (feature_tree), Solid1325 (feature_tree), Solid1326 (feature_tree), Solid1327 (feature_tree), Solid1328 (feature_tree), Solid1329 (feature_tree), Solid1330 (feature_tree), Solid1331 (feature_tree), Solid1332 (feature_tree), Solid1333 (feature_tree), Solid1334 (feature_tree), Solid1335 (feature_tree), Solid1336 (feature_tree), Solid1337 (feature_tree), Solid1338 (feature_tree), Solid1339 (feature_tree), Solid1340 (feature_tree), Solid1341 (feature_tree), Solid1342 (feature_tree), Solid1343 (feature_tree), Solid1344 (feature_tree), Solid1345 (feature_tree), Solid1346 (feature_tree), Solid1347 (feature_tree), Solid1348 (feature_tree), Solid1349 (feature_tree), Solid1350 (feature_tree), Solid1351 (feature_tree), Solid1352 (feature_tree), Solid1353 (feature_tree), Solid1354 (feature_tree), Solid1355 (feature_tree), Solid1356 (feature_tree), Solid1357 (feature_tree), Solid1358 (feature_tree), Solid1359 (feature_tree), Solid1360 (feature_tree), Solid1361 (feature_tree), Solid1362 (feature_tree), Solid1363 (feature_tree), Solid1364 (feature_tree), Solid1365 (feature_tree), Solid1366 (feature_tree), Solid1367 (feature_tree), Solid1368 (feature_tree), Solid1369 (feature_tree), Solid1370 (feature_tree), Solid1371 (feature_tree), Solid1372 (feature_tree), Solid1373 (feature_tree), Solid1374 (feature_tree), Solid1375 (feature_tree), Solid1376 (feature_tree), Solid1377 (feature_tree), Solid1378 (feature_tree), Solid1379 (feature_tree), Solid1380 (feature_tree), Solid1381 (feature_tree), Solid1382 (feature_tree), Solid1383 (feature_tree), Solid1384 (feature_tree), Solid1385 (feature_tree), Solid1386 (feature_tree), Solid1387 (feature_tree), Solid1388 (feature_tree), Solid1389 (feature_tree), Solid1390 (feature_tree), Solid1391 (feature_tree), Solid1392 (feature_tree), Solid1393 (feature_tree), Solid1394 (feature_tree), Solid1395 (feature_tree), Solid1396 (feature_tree), Solid1397 (feature_tree), Solid1398 (feature_tree), Solid1399 (feature_tree), Solid1400 (feature_tree), Solid1401 (feature_tree), Solid1402 (feature_tree), Solid1403 (feature_tree), Solid1404 (feature_tree), Solid1405 (feature_tree), Solid1406 (feature_tree), Solid1407 (feature_tree), Solid1408 (feature_tree), Solid1409 (feature_tree), Solid1410 (feature_tree), Solid1411 (feature_tree), Solid1412 (feature_tree), Solid1413 (feature_tree), Solid1414 (feature_tree), Solid1415 (feature_tree), Solid1416 (feature_tree), Solid1417 (feature_tree), Solid1418 (feature_tree), Solid1419 (feature_tree), Solid1420 (feature_tree), Solid1421 (feature_tree), Solid1422 (feature_tree), Solid1423 (feature_tree), Solid1424 (feature_tree), Solid1425 (feature_tree), Solid1426 (feature_tree), Solid1427 (feature_tree), Solid1428 (feature_tree), Solid1429 (feature_tree), Solid1430 (feature_tree), Solid1431 (feature_tree), Solid1432 (feature_tree), Solid1433 (feature_tree), Solid1434 (feature_tree), Solid1435 (feature_tree), Solid1436 (feature_tree), Solid1437 (feature_tree), Solid1438 (feature_tree), Solid1439 (feature_tree), Solid1440 (feature_tree), Solid1441 (feature_tree), Solid1442 (feature_tree), Solid1443 (feature_tree), Solid1444 (feature_tree), Solid1445 (feature_tree), Solid1446 (feature_tree), Solid1447 (feature_tree), Solid1448 (feature_tree), Solid1449 (feature_tree), Solid1450 (feature_tree), Solid1451 (feature_tree), Solid1452 (feature_tree), Solid1453 (feature_tree), Solid1454 (feature_tree), Solid1455 (feature_tree), Solid1456 (feature_tree), Solid1457 (feature_tree), Solid1458 (feature_tree), Solid1459 (feature_tree), Solid1460 (feature_tree), Solid1461 (feature_tree), Solid1462 (feature_tree), Solid1463 (feature_tree), Solid1464 (feature_tree), Solid1465 (feature_tree), Solid1466 (feature_tree), Solid1467 (feature_tree), Solid1468 (feature_tree), Solid1469 (feature_tree), Solid1470 (feature_tree), Solid1471 (feature_tree), Solid1472 (feature_tree), Solid1473 (feature_tree), Solid1474 (feature_tree), Solid1475 (feature_tree), Solid1476 (feature_tree), Solid1477 (feature_tree), Solid1478 (feature_tree), Solid1479 (feature_tree), Solid1480 (feature_tree), Solid1481 (feature_tree), Solid1482 (feature_tree), Solid1483 (feature_tree), Solid1484 (feature_tree), Solid1485 (feature_tree), Solid1486 (feature_tree), Solid1487 (feature_tree), Solid1488 (feature_tree), Solid1489 (feature_tree), Solid1490 (feature_tree), Solid1491 (feature_tree), Solid1492 (feature_tree), Solid1493 (feature_tree), Solid1494 (feature_tree), Solid1495 (feature_tree), Solid1496 (feature_tree), Solid1497 (feature_tree), Solid1498 (feature_tree), Solid1499 (feature_tree), Solid1500 (feature_tree), Solid1501 (feature_tree), Solid1502 (feature_tree), Solid1503 (feature_tree), Solid1504 (feature_tree), Solid1505 (feature_tree), Solid1506 (feature_tree), Solid1507 (feature_tree), Solid1508 (feature_tree), Solid1509 (feature_tree), Solid1510 (feature_tree), Solid1511 (feature_tree), Solid1512 (feature_tree), Solid1513 (feature_tree), Solid1514 (feature_tree), Solid1515 (feature_tree), Solid1516 (feature_tree), Solid1517 (feature_tree), Solid1518 (feature_tree), Solid1519 (feature_tree), Solid1520 (feature_tree), Solid1521 (feature_tree), Solid1522 (feature_tree), Solid1523 (feature_tree), Solid1524 (feature_tree), Solid1525 (feature_tree), Solid1526 (feature_tree), Solid1527 (feature_tree), Solid1528 (feature_tree), Solid1529 (feature_tree), Solid1530 (feature_tree), Solid1531 (feature_tree), Solid1532 (feature_tree), Solid1533 (feature_tree), Solid1534 (feature_tree), Solid1535 (feature_tree), Solid1536 (feature_tree), Solid1537 (feature_tree), Solid1538 (feature_tree), Solid1539 (feature_tree), Solid1540 (feature_tree), Solid1541 (feature_tree), Solid1542 (feature_tree), Solid1543 (feature_tree), Solid1544 (feature_tree), Solid1545 (feature_tree), Solid1546 (feature_tree), Solid1547 (feature_tree), Solid1548 (feature_tree), Solid1549 (feature_tree), Solid1550 (feature_tree), Solid1551 (feature_tree), Solid1552 (feature_tree), Solid1553 (feature_tree), Solid1554 (feature_tree), Solid1555 (feature_tree), Solid1556 (feature_tree), Solid1557 (feature_tree), Solid1558 (feature_tree), Solid1559 (feature_tree), Solid1560 (feature_tree), Solid1561 (feature_tree), Solid1562 (feature_tree), Solid1563 (feature_tree), Solid1564 (feature_tree), Solid1565 (feature_tree), Solid1566 (feature_tree), Solid1567 (feature_tree), Solid1568 (feature_tree), Solid1569 (feature_tree), Solid1570 (feature_tree), Solid1571 (feature_tree), Solid1572 (feature_tree), Solid1573 (feature_tree), Solid1574 (feature_tree), Solid1575 (feature_tree), Solid1576 (feature_tree), Solid1577 (feature_tree), Solid1578 (feature_tree), Solid1579 (feature_tree), Solid1580 (feature_tree), Solid1581 (feature_tree), Solid1582 (feature_tree), Solid1583 (feature_tree), Solid1584 (feature_tree), Solid1585 (feature_tree), Solid1586 (feature_tree), Solid1587 (feature_tree), Solid1588 (feature_tree), Solid1589 (feature_tree), Solid1590 (feature_tree), Solid1591 (feature_tree), Solid1592 (feature_tree), Solid1593 (feature_tree), Solid1594 (feature_tree), Solid1595 (feature_tree), Solid1596 (feature_tree), Solid1597 (feature_tree), Solid1598 (feature_tree), Solid1599 (feature_tree), Solid1600 (feature_tree), Solid1601 (feature_tree), Solid1602 (feature_tree), Solid1603 (feature_tree), Solid1604 (feature_tree), Solid1605 (feature_tree), Solid1606 (feature_tree), Solid1607 (feature_tree), Solid1608 (feature_tree), Solid1609 (feature_tree), Solid1610 (feature_tree), Solid1611 (feature_tree), Solid1612 (feature_tree), Solid1613 (feature_tree), Solid1614 (feature_tree), Solid1615 (feature_tree), Solid1616 (feature_tree), Solid1617 (feature_tree), Solid1618 (feature_tree), Solid1619 (feature_tree), Solid1620 (feature_tree), Solid1621 (feature_tree), Solid1622 (feature_tree), Solid1623 (feature_tree), Solid1624 (feature_tree), Solid1625 (feature_tree), Solid1626 (feature_tree), Solid1627 (feature_tree), Solid1628 (feature_tree), Solid1629 (feature_tree), Solid1630 (feature_tree), Solid1631 (feature_tree), Solid1632 (feature_tree), Solid1633 (feature_tree), Solid1634 (feature_tree), Solid1635 (feature_tree), Solid1636 (feature_tree), Solid1637 (feature_tree), Solid1638 (feature_tree), Solid1639 (feature_tree), Solid1640 (feature_tree), Solid1641 (feature_tree), Solid1642 (feature_tree), Solid1643 (feature_tree), Solid1644 (feature_tree), Solid1645 (feature_tree), Solid1646 (feature_tree), Solid1647 (feature_tree), Solid1648 (feature_tree), Solid1649 (feature_tree), Solid1650 (feature_tree), Solid1651 (feature_tree), Solid1652 (feature_tree), Solid1653 (feature_tree), Solid1654 (feature_tree), Solid1655 (feature_tree), Solid1656 (feature_tree), Solid1657 (feature_tree), Solid1658 (feature_tree), Solid1659 (feature_tree), Solid1660 (feature_tree), Solid1661 (feature_tree), Solid1662 (feature_tree), Solid1663 (feature_tree), Solid1664 (feature_tree), Solid1665 (feature_tree), Solid1666 (feature_tree), Solid1667 (feature_tree), Solid1668 (feature_tree), Solid1669 (feature_tree), Solid1670 (feature_tree), Solid1671 (feature_tree), Solid1672 (feature_tree), Solid1673 (feature_tree), Solid1674 (feature_tree), Solid1675 (feature_tree), Solid1676 (feature_tree), Solid1677 (feature_tree), Solid1678 (feature_tree), Solid1679 (feature_tree), Solid1680 (feature_tree), Solid1681 (feature_tree), Solid1682 (feature_tree), Solid1683 (feature_tree), Solid1684 (feature_tree), Solid1685 (feature_tree), Solid1686 (feature_tree), Solid1687 (feature_tree), Solid1688 (feature_tree), Solid1689 (feature_tree), Solid1690 (feature_tree), Solid1691 (feature_tree), Solid1692 (feature_tree), Solid1693 (feature_tree), Solid1694 (feature_tree), Solid1695 (feature_tree), Solid1696 (feature_tree), Solid1697 (feature_tree), Solid1698 (feature_tree), Solid1699 (feature_tree), Solid1700 (feature_tree), Solid1701 (feature_tree), Solid1702 (feature_tree), Solid1703 (feature_tree), Solid1704 (feature_tree), Solid1705 (feature_tree), Solid1706 (feature_tree), Solid1707 (feature_tree), Solid1708 (feature_tree), Solid1709 (feature_tree), Solid1710 (feature_tree), Solid1711 (feature_tree), Solid1712 (feature_tree), Solid1713 (feature_tree), Solid1714 (feature_tree), Solid1715 (feature_tree), Solid1716 (feature_tree), Solid1717 (feature_tree), Solid1718 (feature_tree), Solid1719 (feature_tree), Solid1720 (feature_tree), Solid1721 (feature_tree), Solid1722 (feature_tree), Solid1723 (feature_tree), Solid1724 (feature_tree), Solid1725 (feature_tree), Solid1726 (feature_tree), Solid1727 (feature_tree), Solid1728 (feature_tree), Solid1729 (feature_tree), Solid1730 (feature_tree), Solid1731 (feature_tree), Solid1732 (feature_tree), Solid1733 (feature_tree), Solid1734 (feature_tree), Solid1735 (feature_tree), Solid1736 (feature_tree), Solid1737 (feature_tree), Solid1738 (feature_tree), Solid1739 (feature_tree), Solid1740 (feature_tree), Solid1741 (feature_tree), Solid1742 (feature_tree), Solid1743 (feature_tree), Solid1744 (feature_tree), Solid1745 (feature_tree), Solid1746 (feature_tree), Solid1747 (feature_tree), Solid1748 (feature_tree), Solid1749 (feature_tree), Solid1750 (feature_tree), Solid1751 (feature_tree), Solid1752 (feature_tree), Solid1753 (feature_tree), Solid1754 (feature_tree), Solid1755 (feature_tree), Solid1756 (feature_tree), Solid1757 (feature_tree), Solid1758 (feature_tree), Solid1759 (feature_tree), Solid1760 (feature_tree), Solid1761 (feature_tree), Solid1762 (feature_tree), Solid1763 (feature_tree), Solid1764 (feature_tree), Solid1765 (feature_tree), Solid1766 (feature_tree), Solid1767 (feature_tree), Solid1768 (feature_tree), Solid1769 (feature_tree), Solid1770 (feature_tree), Solid1771 (feature_tree), Solid1772 (feature_tree), Solid1773 (feature_tree), Solid1774 (feature_tree), Solid1775 (feature_tree), Solid1776 (feature_tree), Solid1777 (feature_tree), Solid1778 (feature_tree), Solid1779 (feature_tree), Solid1780 (feature_tree), Solid1781 (feature_tree), Solid1782 (feature_tree), Solid1783 (feature_tree), Solid1784 (feature_tree), Solid1785 (feature_tree), Solid1786 (feature_tree), Solid1787 (feature_tree), Solid1788 (feature_tree), Solid1789 (feature_tree), Solid1790 (feature_tree), Solid1791 (feature_tree), Solid1792 (feature_tree), Solid1793 (feature_tree), Solid1794 (feature_tree), Solid1795 (feature_tree), Solid1796 (feature_tree), Solid1797 (feature_tree), Solid1798 (feature_tree), Solid1799 (feature_tree), Solid1800 (feature_tree), Solid1801 (feature_tree), Solid1802 (feature_tree), Solid1803 (feature_tree), Solid1804 (feature_tree), Solid1805 (feature_tree), Solid1806 (feature_tree), Solid1807 (feature_tree), Solid1808 (feature_tree), Solid1809 (feature_tree), Solid1810 (feature_tree), Solid1811 (feature_tree), Solid1812 (feature_tree), Solid1813 (feature_tree), Solid1814 (feature_tree), Solid1815 (feature_tree), Solid1816 (feature_tree), Solid1817 (feature_tree), Solid1818 (feature_tree), Solid1819 (feature_tree), Solid1820 (feature_tree), Solid1821 (feature_tree), Solid1822 (feature_tree), Solid1823 (feature_tree), Solid1824 (feature_tree), Solid1825 (feature_tree), Solid1826 (feature_tree), Solid1827 (feature_tree), Solid1828 (feature_tree), Solid1829 (feature_tree), Solid1830 (feature_tree), Solid1831 (feature_tree), Solid1832 (feature_tree), Solid1833 (feature_tree), Solid1834 (feature_tree), Solid1835 (feature_tree), Solid1836 (feature_tree), Solid1837 (feature_tree), Solid1838 (feature_tree), Solid1839 (feature_tree), Solid1840 (feature_tree), Solid1841 (feature_tree), Solid1842 (feature_tree), Solid1843 (feature_tree), Solid1844 (feature_tree), Solid1845 (feature_tree), Solid1846 (feature_tree), Solid1847 (feature_tree), Solid1848 (feature_tree), Solid1849 (feature_tree), Solid1850 (feature_tree), Solid1851 (feature_tree), Solid1852 (feature_tree), Solid1853 (feature_tree), Solid1854 (feature_tree), Solid1855 (feature_tree), Solid1856 (feature_tree), Solid1857 (feature_tree), Solid1858 (feature_tree), Solid1859 (feature_tree), Solid1860 (feature_tree), Solid1861 (feature_tree), Solid1862 (feature_tree), Solid1863 (feature_tree), Solid1864 (feature_tree), Solid1865 (feature_tree), Solid1866 (feature_tree), Solid1867 (feature_tree), Solid1868 (feature_tree), Solid1869 (feature_tree), Solid1870 (feature_tree), Solid1871 (feature_tree), Solid1872 (feature_tree), Solid1873 (feature_tree), Solid1874 (feature_tree), Solid1875 (feature_tree), Solid1876 (feature_tree), Solid1877 (feature_tree), Solid1878 (feature_tree), Solid1879 (feature_tree), Solid1880 (feature_tree), Solid1881 (feature_tree), Solid1882 (feature_tree), Solid1883 (feature_tree), Solid1884 (feature_tree), Solid1885 (feature_tree), Solid1886 (feature_tree), Solid1887 (feature_tree), Solid1888 (feature_tree), Solid1889 (feature_tree), Solid1890 (feature_tree), Solid1891 (feature_tree), Solid1892 (feature_tree), Solid1893 (feature_tree), Solid1894 (feature_tree), Solid1895 (feature_tree), Solid1896 (feature_tree), Solid1897 (feature_tree), Solid1898 (feature_tree), Solid1899 (feature_tree), Solid1900 (feature_tree), Solid1901 (feature_tree), Solid1902 (feature_tree), Solid1903 (feature_tree), Solid1904 (feature_tree), Solid1905 (feature_tree), Solid1906 (feature_tree), Solid1907 (feature_tree), Solid1908 (feature_tree), Solid1909 (feature_tree), Solid1910 (feature_tree), Solid1911 (feature_tree), Solid1912 (feature_tree), Solid1913 (feature_tree), Solid1914 (feature_tree), Solid1915 (feature_tree), Solid1916 (feature_tree), Solid1917 (feature_tree), Solid1918 (feature_tree), Solid1919 (feature_tree), Solid1920 (feature_tree), Solid1921 (feature_tree), Solid1922 (feature_tree), Solid1923 (feature_tree), Solid1924 (feature_tree), Solid1925 (feature_tree), Solid1926 (feature_tree), Solid1927 (feature_tree), Solid1928 (feature_tree), Solid1929 (feature_tree), Solid1930 (feature_tree), Solid1931 (feature_tree), Solid1932 (feature_tree), Solid1933 (feature_tree), Solid1934 (feature_tree), Solid1935 (feature_tree), Solid1936 (feature_tree), Solid1937 (feature_tree), Solid1938 (feature_tree), Solid1939 (feature_tree), Solid1940 (feature_tree), Solid1941 (feature_tree), Solid1942 (feature_tree), Solid1943 (feature_tree), Solid1944 (feature_tree), Solid1945 (feature_tree), Solid1946 (feature_tree), Solid1947 (feature_tree), Solid1948 (feature_tree), Solid1949 (feature_tree), Solid1950 (feature_tree), Solid1951 (feature_tree), Solid1952 (feature_tree), Solid1953 (feature_tree), Solid1954 (feature_tree), Solid1955 (feature_tree), Solid1956 (feature_tree), Solid1957 (feature_tree), Solid1958 (feature_tree), Solid1959 (feature_tree), Solid1960 (feature_tree), Solid1961 (feature_tree), Solid1962 (feature_tree), Solid1963 (feature_tree), Solid1964 (feature_tree), Solid1965 (feature_tree), Solid1966 (feature_tree), Solid1967 (feature_tree), Solid1968 (feature_tree), Solid1969 (feature_tree), Solid1970 (feature_tree)
feature tree (1972):
  other  "Board_1:1"
  other  "User_Library-0402(1005M)_Cap_2:1"
  other  "User_Library-0402(1005M)_Cap_2:2"
  other  "User_Library-0402(1005M)_Cap_2:3"
  other  "RES-0201(0603mm)_4:1"
  other  "RES-0201(0603mm)_4:2"
  other  "RES-0201(0603mm)_4:3"
  other  "RES-0201(0603mm)_4:4"
  other  "User_Library-0201(0603M)_Cap_6:1"
  other  "User_Library-0201(0603M)_Cap_6:2"
  other  "User_Library-0201(0603M)_Cap_6:3"
  other  "User_Library-0201(0603M)_Cap_8:1"
  other  "User_Library-0201(0603M)_Cap_8:2"
  other  "User_Library-0201(0603M)_Cap_8:3"
  other  "RES-0201(0603mm)_10:1"
  other  "RES-0201(0603mm)_10:2"
  other  "RES-0201(0603mm)_10:3"
  other  "RES-0201(0603mm)_10:4"
  other  "RES-0201(0603mm)_12:1"
  other  "RES-0201(0603mm)_12:2"
  other  "RES-0201(0603mm)_12:3"
  other  "RES-0201(0603mm)_12:4"
  other  "RES-0201(0603mm)_14:1"
  other  "RES-0201(0603mm)_14:2"
  other  "RES-0201(0603mm)_14:3"
  other  "RES-0201(0603mm)_14:4"
  other  "RES-0201(0603mm)_16:1"
  other  "RES-0201(0603mm)_16:2"
  other  "RES-0201(0603mm)_16:3"
  other  "RES-0201(0603mm)_16:4"
  extrude  "Extruded_18:1"  [1 undecoded]
  other  "Cylinder_21:1"
  extrude  "Extruded_23:1"  [1 undecoded]
  other  "RES-0201(0603mm)_26:1"
  other  "RES-0201(0603mm)_26:2"
  other  "RES-0201(0603mm)_26:3"
  other  "RES-0201(0603mm)_26:4"
  other  "RES-0201(0603mm)_28:1"
  other  "RES-0201(0603mm)_28:2"
  other  "RES-0201(0603mm)_28:3"
  other  "RES-0201(0603mm)_28:4"
  other  "RES-0201(0603mm)_30:1"
  other  "RES-0201(0603mm)_30:2"
  other  "RES-0201(0603mm)_30:3"
  other  "RES-0201(0603mm)_30:4"
  other  "RES-0201(0603mm)_32:1"
  other  "RES-0201(0603mm)_32:2"
  other  "RES-0201(0603mm)_32:3"
  other  "RES-0201(0603mm)_32:4"
  other  "RES-0201(0603mm)_34:1"
  other  "RES-0201(0603mm)_34:2"
  other  "RES-0201(0603mm)_34:3"
  other  "RES-0201(0603mm)_34:4"
  other  "RES-0201(0603mm)_36:1"
  other  "RES-0201(0603mm)_36:2"
  other  "RES-0201(0603mm)_36:3"
  other  "RES-0201(0603mm)_36:4"
  other  "RES-0201(0603mm)_38:1"
  other  "RES-0201(0603mm)_38:2"
  other  "RES-0201(0603mm)_38:3"
  other  "RES-0201(0603mm)_38:4"
  other  "RES-0201(0603mm)_40:1"
  other  "RES-0201(0603mm)_40:2"
  other  "RES-0201(0603mm)_40:3"
  other  "RES-0201(0603mm)_40:4"
  other  "RES-0201(0603mm)_42:1"
  other  "RES-0201(0603mm)_42:2"
  other  "RES-0201(0603mm)_42:3"
  other  "RES-0201(0603mm)_42:4"
  other  "RES-0201(0603mm)_44:1"
  other  "RES-0201(0603mm)_44:2"
  other  "RES-0201(0603mm)_44:3"
  other  "RES-0201(0603mm)_44:4"
  other  "RES-0201(0603mm)_46:1"
  other  "RES-0201(0603mm)_46:2"
  other  "RES-0201(0603mm)_46:3"
  other  "RES-0201(0603mm)_46:4"
  other  "RES-0201(0603mm)_48:1"
  other  "RES-0201(0603mm)_48:2"
  other  "RES-0201(0603mm)_48:3"
  other  "RES-0201(0603mm)_48:4"
  other  "RES-0201(0603mm)_50:1"
  other  "RES-0201(0603mm)_50:2"
  other  "RES-0201(0603mm)_50:3"
  other  "RES-0201(0603mm)_50:4"
  other  "RES-0201(0603mm)_52:1"
  other  "RES-0201(0603mm)_52:2"
  other  "RES-0201(0603mm)_52:3"
  other  "RES-0201(0603mm)_52:4"
  other  "RES-0201(0603mm)_54:1"
  other  "RES-0201(0603mm)_54:2"
  other  "RES-0201(0603mm)_54:3"
  other  "RES-0201(0603mm)_54:4"
  other  "RES-0201(0603mm)_56:1"
  other  "RES-0201(0603mm)_56:2"
  other  "RES-0201(0603mm)_56:3"
  other  "RES-0201(0603mm)_56:4"
  other  "RES-0201(0603mm)_58:1"
  other  "RES-0201(0603mm)_58:2"
  other  "RES-0201(0603mm)_58:3"
  other  "RES-0201(0603mm)_58:4"
  other  "RES-0402(1005mm)_60:1"
  other  "RES-0402(1005mm)_60:2"
  other  "RES-0402(1005mm)_60:3"
  other  "RES-0402(1005mm)_60:4"
  other  "RES-0201(0603mm)_62:1"
  other  "RES-0201(0603mm)_62:2"
  other  "RES-0201(0603mm)_62:3"
  other  "RES-0201(0603mm)_62:4"
  other  "RES-0201(0603mm)_64:1"
  other  "RES-0201(0603mm)_64:2"
  other  "RES-0201(0603mm)_64:3"
  other  "RES-0201(0603mm)_64:4"
  other  "RES-0201(0603mm)_66:1"
  other  "RES-0201(0603mm)_66:2"
  other  "RES-0201(0603mm)_66:3"
  other  "RES-0201(0603mm)_66:4"
  other  "RES-0402(1005mm)_68:1"
  other  "RES-0402(1005mm)_68:2"
  other  "RES-0402(1005mm)_68:3"
  other  "RES-0402(1005mm)_68:4"
  other  "RES-0201(0603mm)_70:1"
  other  "RES-0201(0603mm)_70:2"
  other  "RES-0201(0603mm)_70:3"
  other  "RES-0201(0603mm)_70:4"
  other  "RES-0201(0603mm)_72:1"
  other  "RES-0201(0603mm)_72:2"
  other  "RES-0201(0603mm)_72:3"
  other  "RES-0201(0603mm)_72:4"
  other  "CUI_PJ1-021-SMT-TR_74:1"
  other  "CUI_PJ1-021-SMT-TR_74:2"
  other  "CUI_PJ1-021-SMT-TR_74:3"
  other  "CUI_PJ1-021-SMT-TR_74:4"
  other  "CUI_PJ1-021-SMT-TR_74:5"
  other  "CUI_PJ1-021-SMT-TR_74:6"
  other  "User_Library-LTST-C190TBKT_Pad_78:1"
  other  "User_Library-LTST-C190TBKT_Pad005_79:1"
  other  "User_Library-LTST-C190TBKT_Pad001_80:1"
  other  "User_Library-LTST-C190TBKT_Pad001_80:2"
  other  "User_Library-LTST-C190TBKT_Pad004_81:1"
  other  "User_Library-LTST-C190TBKT_Pad003_82:1"
  other  "User_Library-LTST-C190TBKT_Pad003_82:2"
  other  "User_Library-LTST-C190TBKT_Lens_83:1"
  other  "User_Library-0603(1608M)_Cap_86:1"
  other  "User_Library-0603(1608M)_Cap_86:2"
  other  "User_Library-0603(1608M)_Cap_86:3"
  other  "User_Library-0201(0603M)_Cap_88:1"
  other  "User_Library-0201(0603M)_Cap_88:2"
  other  "User_Library-0201(0603M)_Cap_88:3"
  other  "User_Library-0201(0603M)_Cap_90:1"
  other  "User_Library-0201(0603M)_Cap_90:2"
  other  "User_Library-0201(0603M)_Cap_90:3"
  other  "User_Library-1210(3225M)_Cap_92:1"
  other  "User_Library-1210(3225M)_Cap_92:2"
  other  "User_Library-1210(3225M)_Cap_92:3"
  other  "User_Library-0201(0603M)_Cap_94:1"
  other  "User_Library-0201(0603M)_Cap_94:2"
  other  "User_Library-0201(0603M)_Cap_94:3"
  other  "User_Library-0603(1608M)_Cap_96:1"
  other  "User_Library-0603(1608M)_Cap_96:2"
  other  "User_Library-0603(1608M)_Cap_96:3"
  other  "RES-0201(0603mm)_98:1"
  other  "RES-0201(0603mm)_98:2"
  other  "RES-0201(0603mm)_98:3"
  other  "RES-0201(0603mm)_98:4"
  other  "RES-0201(0603mm)_100:1"
  other  "RES-0201(0603mm)_100:2"
  other  "RES-0201(0603mm)_100:3"
  other  "RES-0201(0603mm)_100:4"
  other  "RES-0201(0603mm)_102:1"
  other  "RES-0201(0603mm)_102:2"
  other  "RES-0201(0603mm)_102:3"
  other  "RES-0201(0603mm)_102:4"
  other  "RES-0402(1005mm)_104:1"
  other  "RES-0402(1005mm)_104:2"
  other  "RES-0402(1005mm)_104:3"
  other  "RES-0402(1005mm)_104:4"
  other  "RES-0201(0603mm)_106:1"
  other  "RES-0201(0603mm)_106:2"
  other  "RES-0201(0603mm)_106:3"
  other  "RES-0201(0603mm)_106:4"
  other  "RES-0402(1005mm)_108:1"
  other  "RES-0402(1005mm)_108:2"
  other  "RES-0402(1005mm)_108:3"
  other  "RES-0402(1005mm)_108:4"
  other  "RES-0402(1005mm)_110:1"
  other  "RES-0402(1005mm)_110:2"
  other  "RES-0402(1005mm)_110:3"
  other  "RES-0402(1005mm)_110:4"
  other  "RES-0201(0603mm)_112:1"
  other  "RES-0201(0603mm)_112:2"
  other  "RES-0201(0603mm)_112:3"
  other  "RES-0201(0603mm)_112:4"
  extrude  "Extruded_114:1"  [1 undecoded]
  other  "Cylinder_117:1"
  extrude  "Extruded_119:1"  [1 undecoded]
  other  "Cylinder_122:1"
  extrude  "Extruded_124:1"  [1 undecoded]
  extrude  "Extruded_127:1"  [1 undecoded]
  other  "Cylinder_129:1"
  extrude  "Extruded_131:1"  [1 undecoded]
  extrude  "Extruded_134:1"  [1 undecoded]
  extrude  "Extruded_137:1"  [1 undecoded]
  extrude  "Extruded_137:2"  [1 undecoded]
  extrude  "Extruded_142:1"  [1 undecoded]
  other  "CircuitWorks-SOT-23-5_145:1"
  other  "User_Library-VQFN-32_147:1"
  extrude  "Extruded_149:1"  [1 undecoded]
  other  "Open_CASCADE_STEP_translator_6.8_17.2.1_153:1"
  other  "Thermal_Shape_155:1"
  other  "Open_CASCADE_STEP_translator_6.8_17.4.1_156:1"
  other  "Open_CASCADE_STEP_translator_6.8_17.4.1_156:2"
  other  "Open_CASCADE_STEP_translator_6.8_17.4.1_156:3"
  other  "Open_CASCADE_STEP_translator_6.8_17.4.1_156:4"
  other  "Open_CASCADE_STEP_translator_6.8_17.4.1_156:5"
  other  "Open_CASCADE_STEP_translator_6.8_17.4.1_156:6"
  other  "Open_CASCADE_STEP_translator_6.8_17.4.1_156:7"
  other  "Open_CASCADE_STEP_translator_6.8_17.4.1_156:8"
  other  "Open_CASCADE_STEP_translator_6.8_17.4.1_156:9"
  other  "Open_CASCADE_STEP_translator_6.8_17.4.1_156:10"
  other  "Open_CASCADE_STEP_translator_6.8_17.4.1_156:11"
  other  "Open_CASCADE_STEP_translator_6.8_17.4.1_156:12"
  other  "Open_CASCADE_STEP_translator_6.8_17.4.1_156:13"
  other  "Open_CASCADE_STEP_translator_6.8_17.4.1_156:14"
  other  "Open_CASCADE_STEP_translator_6.8_17.4.1_156:15"
  other  "Open_CASCADE_STEP_translator_6.8_17.4.1_156:16"
  other  "Open_CASCADE_STEP_translator_6.8_17.4.1_156:17"
  other  "Open_CASCADE_STEP_translator_6.8_17.4.1_156:18"
  other  "Open_CASCADE_STEP_translator_6.8_17.4.1_156:19"
  other  "Open_CASCADE_STEP_translator_6.8_17.4.1_156:20"
  other  "Open_CASCADE_STEP_translator_6.8_17.4.1_156:21"
  other  "Open_CASCADE_STEP_translator_6.8_17.4.1_156:22"
  other  "Open_CASCADE_STEP_translator_6.8_17.4.1_156:23"
  other  "Open_CASCADE_STEP_translator_6.8_17.4.1_156:24"
  other  "Open_CASCADE_STEP_translator_6.8_17.4.1_156:25"
  other  "Open_CASCADE_STEP_translator_6.8_17.4.1_156:26"
  other  "Open_CASCADE_STEP_translator_6.8_17.4.1_156:27"
  other  "Open_CASCADE_STEP_translator_6.8_17.4.1_156:28"
  other  "Open_CASCADE_STEP_translator_6.8_17.4.1_156:29"
  other  "Open_CASCADE_STEP_translator_6.8_17.4.1_156:30"
  other  "Open_CASCADE_STEP_translator_6.8_17.4.1_156:31"
  other  "Open_CASCADE_STEP_translator_6.8_17.4.1_156:32"
  other  "Open_CASCADE_STEP_translator_6.8_17.4.1_156:33"
  other  "Open_CASCADE_STEP_translator_6.8_17.4.1_156:34"
  other  "Open_CASCADE_STEP_translator_6.8_17.4.1_156:35"
  other  "Open_CASCADE_STEP_translator_6.8_17.4.1_156:36"
  other  "Open_CASCADE_STEP_translator_6.8_17.4.1_156:37"
  other  "Open_CASCADE_STEP_translator_6.8_17.4.1_156:38"
  other  "Open_CASCADE_STEP_translator_6.8_17.4.1_156:39"
  other  "Open_CASCADE_STEP_translator_6.8_17.4.1_156:40"
  other  "Open_CASCADE_STEP_translator_6.8_17.4.1_156:41"
  other  "Open_CASCADE_STEP_translator_6.8_17.4.1_156:42"
  other  "Open_CASCADE_STEP_translator_6.8_17.4.1_156:43"
  other  "Open_CASCADE_STEP_translator_6.8_17.4.1_156:44"
  other  "Open_CASCADE_STEP_translator_6.8_17.4.1_156:45"
  other  "Open_CASCADE_STEP_translator_6.8_17.4.1_156:46"
  other  "Open_CASCADE_STEP_translator_6.8_17.4.1_156:47"
  other  "Open_CASCADE_STEP_translator_6.8_17.4.1_156:48"
  other  "Open_CASCADE_STEP_translator_6.8_17.4.1_156:49"
  other  "Open_CASCADE_STEP_translator_6.8_17.4.1_156:50"
  other  "Open_CASCADE_STEP_translator_6.8_17.4.1_156:51"
  other  "Open_CASCADE_STEP_translator_6.8_17.4.1_156:52"
  other  "Open_CASCADE_STEP_translator_6.8_17.4.1_156:53"
  other  "Open_CASCADE_STEP_translator_6.8_17.4.1_156:54"
  other  "Open_CASCADE_STEP_translator_6.8_17.4.1_156:55"
  other  "Open_CASCADE_STEP_translator_6.8_17.4.1_156:56"
  other  "Open_CASCADE_STEP_translator_6.8_17.2.1_216:1"
  other  "Thermal_Shape_218:1"
  other  "Open_CASCADE_STEP_translator_6.8_17.4.1_219:1"
  other  "Open_CASCADE_STEP_translator_6.8_17.4.1_219:2"
  other  "Open_CASCADE_STEP_translator_6.8_17.4.1_219:3"
  other  "Open_CASCADE_STEP_translator_6.8_17.4.1_219:4"
  other  "Open_CASCADE_STEP_translator_6.8_17.4.1_219:5"
  other  "Open_CASCADE_STEP_translator_6.8_17.4.1_219:6"
  other  "Open_CASCADE_STEP_translator_6.8_17.4.1_219:7"
  other  "Open_CASCADE_STEP_translator_6.8_17.4.1_219:8"
  other  "Open_CASCADE_STEP_translator_6.8_17.4.1_219:9"
  other  "Open_CASCADE_STEP_translator_6.8_17.4.1_219:10"
  other  "Open_CASCADE_STEP_translator_6.8_17.4.1_219:11"
  other  "Open_CASCADE_STEP_translator_6.8_17.4.1_219:12"
  other  "Open_CASCADE_STEP_translator_6.8_17.4.1_219:13"
  other  "Open_CASCADE_STEP_translator_6.8_17.4.1_219:14"
  other  "Open_CASCADE_STEP_translator_6.8_17.4.1_219:15"
  other  "Open_CASCADE_STEP_translator_6.8_17.4.1_219:16"
  other  "Open_CASCADE_STEP_translator_6.8_17.4.1_219:17"
  other  "Open_CASCADE_STEP_translator_6.8_17.4.1_219:18"
  other  "Open_CASCADE_STEP_translator_6.8_17.4.1_219:19"
  other  "Open_CASCADE_STEP_translator_6.8_17.4.1_219:20"
  other  "Open_CASCADE_STEP_translator_6.8_17.4.1_219:21"
  other  "Open_CASCADE_STEP_translator_6.8_17.4.1_219:22"
  other  "Open_CASCADE_STEP_translator_6.8_17.4.1_219:23"
  other  "Open_CASCADE_STEP_translator_6.8_17.4.1_219:24"
  other  "Open_CASCADE_STEP_translator_6.8_17.4.1_219:25"
  other  "Open_CASCADE_STEP_translator_6.8_17.4.1_219:26"
  other  "Open_CASCADE_STEP_translator_6.8_17.4.1_219:27"
  other  "Open_CASCADE_STEP_translator_6.8_17.4.1_219:28"
  other  "Open_CASCADE_STEP_translator_6.8_17.4.1_219:29"
  other  "Open_CASCADE_STEP_translator_6.8_17.4.1_219:30"
  other  "Open_CASCADE_STEP_translator_6.8_17.4.1_219:31"
  other  "Open_CASCADE_STEP_translator_6.8_17.4.1_219:32"
  other  "Open_CASCADE_STEP_translator_6.8_17.4.1_219:33"
  other  "Open_CASCADE_STEP_translator_6.8_17.4.1_219:34"
  other  "Open_CASCADE_STEP_translator_6.8_17.4.1_219:35"
  other  "Open_CASCADE_STEP_translator_6.8_17.4.1_219:36"
  other  "Open_CASCADE_STEP_translator_6.8_17.4.1_219:37"
  other  "Open_CASCADE_STEP_translator_6.8_17.4.1_219:38"
  other  "Open_CASCADE_STEP_translator_6.8_17.4.1_219:39"
  other  "Open_CASCADE_STEP_translator_6.8_17.4.1_219:40"
  other  "Open_CASCADE_STEP_translator_6.8_17.4.1_219:41"
  other  "Open_CASCADE_STEP_translator_6.8_17.4.1_219:42"
  other  "Open_CASCADE_STEP_translator_6.8_17.4.1_219:43"
  other  "Open_CASCADE_STEP_translator_6.8_17.4.1_219:44"
  other  "Open_CASCADE_STEP_translator_6.8_17.4.1_219:45"
  other  "Open_CASCADE_STEP_translator_6.8_17.4.1_219:46"
  other  "Open_CASCADE_STEP_translator_6.8_17.4.1_219:47"
  other  "Open_CASCADE_STEP_translator_6.8_17.4.1_219:48"
  other  "Open_CASCADE_STEP_translator_6.8_17.4.1_219:49"
  other  "Open_CASCADE_STEP_translator_6.8_17.4.1_219:50"
  other  "Open_CASCADE_STEP_translator_6.8_17.4.1_219:51"
  other  "Open_CASCADE_STEP_translator_6.8_17.4.1_219:52"
  other  "Open_CASCADE_STEP_translator_6.8_17.4.1_219:53"
  other  "Open_CASCADE_STEP_translator_6.8_17.4.1_219:54"
  other  "Open_CASCADE_STEP_translator_6.8_17.4.1_219:55"
  other  "Open_CASCADE_STEP_translator_6.8_17.4.1_219:56"
  extrude  "Extruded_278:1"  [1 undecoded]
  other  "User_Library-tssop14-2_281:1"
  other  "User_Library-tssop14-2_281:2"
  other  "User_Library-tssop14-2_281:3"
  extrude  "Extruded_283:1"  [1 undecoded]
  extrude  "Extruded_286:1"  [1 undecoded]
  extrude  "Extruded_289:1"  [1 undecoded]
  other  "User_Library-VQFN-32_292:1"
  other  "User_Library-QFN24_height=0_55_Part_QFN24_4x4_294:1"
  other  "User_Library-QFN24_height=0_55_Part_QFN24_4x4_294:2"
  other  "User_Library-QFN24_height=0_55_Fuss_QFN24______________295:1"
  other  "User_Library-QFN24_height=0_55_Fuss_QFN24______________296:1"
  other  "User_Library-QFN24_height=0_55_Fuss_QFN24______________297:1"
  other  "User_Library-QFN24_height=0_55_Fuss_QFN24______________298:1"
  other  "User_Library-QFN24_height=0_55_Fuss_QFN24______________299:1"
  other  "User_Library-QFN24_height=0_55_Fuss_QFN24______________300:1"
  other  "User_Library-QFN24_height=0_55_Fuss_QFN24______________301:1"
  other  "User_Library-QFN24_height=0_55_Fuss_QFN24______________302:1"
  other  "User_Library-QFN24_height=0_55_Fuss_QFN24______________303:1"
  other  "User_Library-QFN24_height=0_55_Fuss_QFN24______________304:1"
  other  "User_Library-QFN24_height=0_55_Fuss_QFN24______________305:1"
  other  "User_Library-QFN24_height=0_55_Fuss_QFN24______________306:1"
  other  "User_Library-QFN24_height=0_55_Fuss_QFN24______________295:2"
  other  "User_Library-QFN24_height=0_55_Fuss_QFN24______________296:2"
  other  "User_Library-QFN24_height=0_55_Fuss_QFN24______________297:2"
  other  "User_Library-QFN24_height=0_55_Fuss_QFN24______________298:2"
  other  "User_Library-QFN24_height=0_55_Fuss_QFN24______________299:2"
  other  "User_Library-QFN24_height=0_55_Fuss_QFN24______________300:2"
  other  "User_Library-QFN24_height=0_55_Fuss_QFN24______________301:2"
  other  "User_Library-QFN24_height=0_55_Fuss_QFN24______________302:2"
  other  "User_Library-QFN24_height=0_55_Fuss_QFN24______________303:2"
  other  "User_Library-QFN24_height=0_55_Fuss_QFN24______________304:2"
  other  "User_Library-QFN24_height=0_55_Fuss_QFN24______________305:2"
  other  "User_Library-QFN24_height=0_55_Fuss_QFN24______________306:2"
  other  "User_Library-QFN24_height=0_55_Fuss_QFN24______________295:3"
  other  "User_Library-QFN24_height=0_55_Fuss_QFN24______________296:3"
  other  "User_Library-QFN24_height=0_55_Fuss_QFN24______________297:3"
  other  "User_Library-QFN24_height=0_55_Fuss_QFN24______________298:3"
  other  "User_Library-QFN24_height=0_55_Fuss_QFN24______________299:3"
  other  "User_Library-QFN24_height=0_55_Fuss_QFN24______________300:3"
  other  "User_Library-QFN24_height=0_55_Fuss_QFN24______________301:3"
  other  "User_Library-QFN24_height=0_55_Fuss_QFN24______________302:3"
  other  "User_Library-QFN24_height=0_55_Fuss_QFN24______________303:3"
  other  "User_Library-QFN24_height=0_55_Fuss_QFN24______________304:3"
  other  "User_Library-QFN24_height=0_55_Fuss_QFN24______________305:3"
  other  "User_Library-QFN24_height=0_55_Fuss_QFN24______________306:3"
  other  "User_Library-QFN24_height=0_55_Fuss_QFN24______________295:4"
  other  "User_Library-QFN24_height=0_55_Fuss_QFN24______________296:4"
  other  "User_Library-QFN24_height=0_55_Fuss_QFN24______________297:4"
  other  "User_Library-QFN24_height=0_55_Fuss_QFN24______________298:4"
  other  "User_Library-QFN24_height=0_55_Fuss_QFN24______________299:4"
  other  "User_Library-QFN24_height=0_55_Fuss_QFN24______________300:4"
  other  "User_Library-QFN24_height=0_55_Fuss_QFN24______________301:4"
  other  "User_Library-QFN24_height=0_55_Fuss_QFN24______________302:4"
  other  "User_Library-QFN24_height=0_55_Fuss_QFN24______________303:4"
  other  "User_Library-QFN24_height=0_55_Fuss_QFN24______________304:4"
  other  "User_Library-QFN24_height=0_55_Fuss_QFN24______________305:4"
  other  "User_Library-QFN24_height=0_55_Fuss_QFN24______________306:4"
  extrude  "Extruded_313:1"  [1 undecoded]
  other  "PTS810SJG250SMTRLFS_316:1"
  extrude  "Extruded_318:1"  [1 undecoded]
  other  "PTS810SJG250SMTRLFS_321:1"
  other  "PTS810SJG250SMTRLFS_323:1"
  other  "RES-0402(1005mm)_325:1"
  other  "RES-0402(1005mm)_325:2"
  other  "RES-0402(1005mm)_325:3"
  other  "RES-0402(1005mm)_325:4"
  other  "RES-0201(0603mm)_327:1"
  other  "RES-0201(0603mm)_327:2"
  other  "RES-0201(0603mm)_327:3"
  other  "RES-0201(0603mm)_327:4"
  other  "RES-0201(0603mm)_329:1"
  other  "RES-0201(0603mm)_329:2"
  other  "RES-0201(0603mm)_329:3"
  other  "RES-0201(0603mm)_329:4"
  other  "RES-0201(0603mm)_331:1"
  other  "RES-0201(0603mm)_331:2"
  other  "RES-0201(0603mm)_331:3"
  other  "RES-0201(0603mm)_331:4"
  other  "RES-0201(0603mm)_333:1"
  other  "RES-0201(0603mm)_333:2"
  other  "RES-0201(0603mm)_333:3"
  other  "RES-0201(0603mm)_333:4"
  other  "RES-0201(0603mm)_335:1"
  other  "RES-0201(0603mm)_335:2"
  other  "RES-0201(0603mm)_335:3"
  other  "RES-0201(0603mm)_335:4"
  other  "RES-0201(0603mm)_337:1"
  other  "RES-0201(0603mm)_337:2"
  other  "RES-0201(0603mm)_337:3"
  other  "RES-0201(0603mm)_337:4"
  other  "RES-0201(0603mm)_339:1"
  other  "RES-0201(0603mm)_339:2"
  other  "RES-0201(0603mm)_339:3"
  other  "RES-0201(0603mm)_339:4"
  other  "RES-0402(1005mm)_341:1"
  other  "RES-0402(1005mm)_341:2"
  other  "RES-0402(1005mm)_341:3"
  other  "RES-0402(1005mm)_341:4"
  other  "RES-0201(0603mm)_343:1"
  other  "RES-0201(0603mm)_343:2"
  other  "RES-0201(0603mm)_343:3"
  other  "RES-0201(0603mm)_343:4"
  other  "RES-0201(0603mm)_345:1"
  other  "RES-0201(0603mm)_345:2"
  other  "RES-0201(0603mm)_345:3"
  other  "RES-0201(0603mm)_345:4"
  other  "RES-0201(0603mm)_347:1"
  other  "RES-0201(0603mm)_347:2"
  other  "RES-0201(0603mm)_347:3"
  other  "RES-0201(0603mm)_347:4"
  other  "RES-0402(1005mm)_349:1"
  other  "RES-0402(1005mm)_349:2"
  other  "RES-0402(1005mm)_349:3"
  other  "RES-0402(1005mm)_349:4"
  other  "RES-0201(0603mm)_351:1"
  other  "RES-0201(0603mm)_351:2"
  other  "RES-0201(0603mm)_351:3"
  other  "RES-0201(0603mm)_351:4"
  other  "RES-0201(0603mm)_353:1"
  other  "RES-0201(0603mm)_353:2"
  other  "RES-0201(0603mm)_353:3"
  other  "RES-0201(0603mm)_353:4"
  other  "RES-0402(1005mm)_355:1"
  other  "RES-0402(1005mm)_355:2"
  other  "RES-0402(1005mm)_355:3"
  other  "RES-0402(1005mm)_355:4"
  other  "RES-0201(0603mm)_357:1"
  other  "RES-0201(0603mm)_357:2"
  other  "RES-0201(0603mm)_357:3"
  other  "RES-0201(0603mm)_357:4"
  other  "RES-0402(1005mm)_359:1"
  other  "RES-0402(1005mm)_359:2"
  other  "RES-0402(1005mm)_359:3"
  other  "RES-0402(1005mm)_359:4"
  other  "RES-0402(1005mm)_361:1"
  other  "RES-0402(1005mm)_361:2"
  other  "RES-0402(1005mm)_361:3"
  other  "RES-0402(1005mm)_361:4"
  other  "RES-0402(1005mm)_363:1"
  other  "RES-0402(1005mm)_363:2"
  other  "RES-0402(1005mm)_363:3"
  other  "RES-0402(1005mm)_363:4"
  other  "RES-0201(0603mm)_365:1"
  other  "RES-0201(0603mm)_365:2"
  other  "RES-0201(0603mm)_365:3"
  other  "RES-0201(0603mm)_365:4"
  other  "RES-0201(0603mm)_367:1"
  other  "RES-0201(0603mm)_367:2"
  other  "RES-0201(0603mm)_367:3"
  other  "RES-0201(0603mm)_367:4"
  other  "RES-0402(1005mm)_369:1"
  other  "RES-0402(1005mm)_369:2"
  other  "RES-0402(1005mm)_369:3"
  other  "RES-0402(1005mm)_369:4"
  other  "RES-0201(0603mm)_371:1"
  other  "RES-0201(0603mm)_371:2"
  other  "RES-0201(0603mm)_371:3"
  other  "RES-0201(0603mm)_371:4"
  other  "RES-0201(0603mm)_373:1"
  other  "RES-0201(0603mm)_373:2"
  other  "RES-0201(0603mm)_373:3"
  other  "RES-0201(0603mm)_373:4"
  other  "RES-0201(0603mm)_375:1"
  other  "RES-0201(0603mm)_375:2"
  other  "RES-0201(0603mm)_375:3"
  other  "RES-0201(0603mm)_375:4"
  other  "RES-0201(0603mm)_377:1"
  other  "RES-0201(0603mm)_377:2"
  other  "RES-0201(0603mm)_377:3"
  other  "RES-0201(0603mm)_377:4"
  other  "RES-0201(0603mm)_379:1"
  other  "RES-0201(0603mm)_379:2"
  other  "RES-0201(0603mm)_379:3"
  other  "RES-0201(0603mm)_379:4"
  other  "RES-0201(0603mm)_381:1"
  other  "RES-0201(0603mm)_381:2"
  other  "RES-0201(0603mm)_381:3"
  other  "RES-0201(0603mm)_381:4"
  other  "RES-0402(1005mm)_383:1"
  other  "RES-0402(1005mm)_383:2"
  other  "RES-0402(1005mm)_383:3"
  other  "RES-0402(1005mm)_383:4"
  other  "RES-0201(0603mm)_385:1"
  other  "RES-0201(0603mm)_385:2"
  other  "RES-0201(0603mm)_385:3"
  other  "RES-0201(0603mm)_385:4"
  other  "RES-0201(0603mm)_387:1"
  other  "RES-0201(0603mm)_387:2"
  other  "RES-0201(0603mm)_387:3"
  other  "RES-0201(0603mm)_387:4"
  other  "RES-0201(0603mm)_389:1"
  other  "RES-0201(0603mm)_389:2"
  other  "RES-0201(0603mm)_389:3"
  other  "RES-0201(0603mm)_389:4"
  other  "RES-0201(0603mm)_391:1"
  other  "RES-0201(0603mm)_391:2"
  other  "RES-0201(0603mm)_391:3"
  other  "RES-0201(0603mm)_391:4"
  other  "RES-0201(0603mm)_393:1"
  other  "RES-0201(0603mm)_393:2"
  other  "RES-0201(0603mm)_393:3"
  other  "RES-0201(0603mm)_393:4"
  other  "RES-0201(0603mm)_395:1"
  other  "RES-0201(0603mm)_395:2"
  other  "RES-0201(0603mm)_395:3"
  other  "RES-0201(0603mm)_395:4"
  other  "RES-0201(0603mm)_397:1"
  other  "RES-0201(0603mm)_397:2"
  other  "RES-0201(0603mm)_397:3"
  other  "RES-0201(0603mm)_397:4"
  other  "RES-0201(0603mm)_399:1"
  other  "RES-0201(0603mm)_399:2"
  other  "RES-0201(0603mm)_399:3"
  other  "RES-0201(0603mm)_399:4"
  other  "RES-0201(0603mm)_401:1"
  other  "RES-0201(0603mm)_401:2"
  other  "RES-0201(0603mm)_401:3"
  other  "RES-0201(0603mm)_401:4"
  other  "RES-0201(0603mm)_403:1"
  other  "RES-0201(0603mm)_403:2"
  other  "RES-0201(0603mm)_403:3"
  other  "RES-0201(0603mm)_403:4"
  other  "RES-0201(0603mm)_405:1"
  other  "RES-0201(0603mm)_405:2"
  other  "RES-0201(0603mm)_405:3"
  other  "RES-0201(0603mm)_405:4"
  other  "RES-0201(0603mm)_407:1"
  other  "RES-0201(0603mm)_407:2"
  other  "RES-0201(0603mm)_407:3"
  other  "RES-0201(0603mm)_407:4"
  other  "RES-0201(0603mm)_409:1"
  other  "RES-0201(0603mm)_409:2"
  other  "RES-0201(0603mm)_409:3"
  other  "RES-0201(0603mm)_409:4"
  other  "RES-0201(0603mm)_411:1"
  other  "RES-0201(0603mm)_411:2"
  other  "RES-0201(0603mm)_411:3"
  other  "RES-0201(0603mm)_411:4"
  other  "RES-0201(0603mm)_413:1"
  other  "RES-0201(0603mm)_413:2"
  other  "RES-0201(0603mm)_413:3"
  other  "RES-0201(0603mm)_413:4"
  other  "RES-0201(0603mm)_415:1"
  other  "RES-0201(0603mm)_415:2"
  other  "RES-0201(0603mm)_415:3"
  other  "RES-0201(0603mm)_415:4"
  other  "RES-0201(0603mm)_417:1"
  other  "RES-0201(0603mm)_417:2"
  other  "RES-0201(0603mm)_417:3"
  other  "RES-0201(0603mm)_417:4"
  other  "RES-0201(0603mm)_419:1"
  other  "RES-0201(0603mm)_419:2"
  other  "RES-0201(0603mm)_419:3"
  other  "RES-0201(0603mm)_419:4"
  other  "RES-0201(0603mm)_421:1"
  other  "RES-0201(0603mm)_421:2"
  other  "RES-0201(0603mm)_421:3"
  other  "RES-0201(0603mm)_421:4"
  other  "RES-0201(0603mm)_423:1"
  other  "RES-0201(0603mm)_423:2"
  other  "RES-0201(0603mm)_423:3"
  other  "RES-0201(0603mm)_423:4"
  other  "RES-0201(0603mm)_425:1"
  other  "RES-0201(0603mm)_425:2"
  other  "RES-0201(0603mm)_425:3"
  other  "RES-0201(0603mm)_425:4"
  other  "RES-0201(0603mm)_427:1"
  other  "RES-0201(0603mm)_427:2"
  other  "RES-0201(0603mm)_427:3"
  other  "RES-0201(0603mm)_427:4"
  other  "RES-0201(0603mm)_429:1"
  other  "RES-0201(0603mm)_429:2"
  other  "RES-0201(0603mm)_429:3"
  other  "RES-0201(0603mm)_429:4"
  other  "RES-0201(0603mm)_431:1"
  other  "RES-0201(0603mm)_431:2"
  other  "RES-0201(0603mm)_431:3"
  other  "RES-0201(0603mm)_431:4"
  other  "RES-0201(0603mm)_433:1"
  other  "RES-0201(0603mm)_433:2"
  other  "RES-0201(0603mm)_433:3"
  other  "RES-0201(0603mm)_433:4"
  other  "RES-0201(0603mm)_435:1"
  other  "RES-0201(0603mm)_435:2"
  other  "RES-0201(0603mm)_435:3"
  other  "RES-0201(0603mm)_435:4"
  other  "RES-0201(0603mm)_437:1"
  other  "RES-0201(0603mm)_437:2"
  other  "RES-0201(0603mm)_437:3"
  other  "RES-0201(0603mm)_437:4"
  other  "RES-0201(0603mm)_439:1"
  other  "RES-0201(0603mm)_439:2"
  other  "RES-0201(0603mm)_439:3"
  other  "RES-0201(0603mm)_439:4"
  other  "RES-0201(0603mm)_441:1"
  other  "RES-0201(0603mm)_441:2"
  other  "RES-0201(0603mm)_441:3"
  other  "RES-0201(0603mm)_441:4"
  other  "RES-0201(0603mm)_443:1"
  other  "RES-0201(0603mm)_443:2"
  other  "RES-0201(0603mm)_443:3"
  other  "RES-0201(0603mm)_443:4"
  other  "RES-0201(0603mm)_445:1"
  other  "RES-0201(0603mm)_445:2"
  other  "RES-0201(0603mm)_445:3"
  other  "RES-0201(0603mm)_445:4"
  other  "RES-0201(0603mm)_447:1"
  other  "RES-0201(0603mm)_447:2"
  other  "RES-0201(0603mm)_447:3"
  other  "RES-0201(0603mm)_447:4"
  other  "RES-0201(0603mm)_449:1"
  other  "RES-0201(0603mm)_449:2"
  other  "RES-0201(0603mm)_449:3"
  other  "RES-0201(0603mm)_449:4"
  other  "RES-0201(0603mm)_451:1"
  other  "RES-0201(0603mm)_451:2"
  other  "RES-0201(0603mm)_451:3"
  other  "RES-0201(0603mm)_451:4"
  other  "RES-0201(0603mm)_453:1"
  other  "RES-0201(0603mm)_453:2"
  other  "RES-0201(0603mm)_453:3"
  other  "RES-0201(0603mm)_453:4"
  other  "RES-0201(0603mm)_455:1"
  other  "RES-0201(0603mm)_455:2"
  other  "RES-0201(0603mm)_455:3"
  other  "RES-0201(0603mm)_455:4"
  other  "RES-0201(0603mm)_457:1"
  other  "RES-0201(0603mm)_457:2"
  other  "RES-0201(0603mm)_457:3"
  other  "RES-0201(0603mm)_457:4"
  other  "RES-0201(0603mm)_459:1"
  other  "RES-0201(0603mm)_459:2"
  other  "RES-0201(0603mm)_459:3"
  other  "RES-0201(0603mm)_459:4"
  other  "RES-0201(0603mm)_461:1"
  other  "RES-0201(0603mm)_461:2"
  other  "RES-0201(0603mm)_461:3"
  other  "RES-0201(0603mm)_461:4"
  other  "RES-0201(0603mm)_463:1"
  other  "RES-0201(0603mm)_463:2"
  other  "RES-0201(0603mm)_463:3"
  other  "RES-0201(0603mm)_463:4"
  other  "RES-0201(0603mm)_465:1"
  other  "RES-0201(0603mm)_465:2"
  other  "RES-0201(0603mm)_465:3"
  other  "RES-0201(0603mm)_465:4"
  other  "RES-0201(0603mm)_467:1"
  other  "RES-0201(0603mm)_467:2"
  other  "RES-0201(0603mm)_467:3"
  other  "RES-0201(0603mm)_467:4"
  other  "RES-0201(0603mm)_469:1"
  other  "RES-0201(0603mm)_469:2"
  other  "RES-0201(0603mm)_469:3"
  other  "RES-0201(0603mm)_469:4"
  other  "RES-0201(0603mm)_471:1"
  other  "RES-0201(0603mm)_471:2"
  other  "RES-0201(0603mm)_471:3"
  other  "RES-0201(0603mm)_471:4"
  other  "RES-0201(0603mm)_473:1"
  other  "RES-0201(0603mm)_473:2"
  other  "RES-0201(0603mm)_473:3"
  other  "RES-0201(0603mm)_473:4"
  other  "RES-0201(0603mm)_475:1"
  other  "RES-0201(0603mm)_475:2"
  other  "RES-0201(0603mm)_475:3"
  other  "RES-0201(0603mm)_475:4"
  other  "RES-0201(0603mm)_477:1"
  other  "RES-0201(0603mm)_477:2"
  other  "RES-0201(0603mm)_477:3"
  other  "RES-0201(0603mm)_477:4"
  other  "RES-0201(0603mm)_479:1"
  other  "RES-0201(0603mm)_479:2"
  other  "RES-0201(0603mm)_479:3"
  other  "RES-0201(0603mm)_479:4"
  other  "RES-0201(0603mm)_481:1"
  other  "RES-0201(0603mm)_481:2"
  other  "RES-0201(0603mm)_481:3"
  other  "RES-0201(0603mm)_481:4"
  other  "RES-0201(0603mm)_483:1"
  other  "RES-0201(0603mm)_483:2"
  other  "RES-0201(0603mm)_483:3"
  other  "RES-0201(0603mm)_483:4"
  other  "RES-0201(0603mm)_485:1"
  other  "RES-0201(0603mm)_485:2"
  other  "RES-0201(0603mm)_485:3"
  other  "RES-0201(0603mm)_485:4"
  other  "RES-0201(0603mm)_487:1"
  other  "RES-0201(0603mm)_487:2"
  other  "RES-0201(0603mm)_487:3"
  other  "RES-0201(0603mm)_487:4"
  other  "RES-0201(0603mm)_489:1"
  other  "RES-0201(0603mm)_489:2"
  other  "RES-0201(0603mm)_489:3"
  other  "RES-0201(0603mm)_489:4"
  other  "RES-0201(0603mm)_491:1"
  other  "RES-0201(0603mm)_491:2"
  other  "RES-0201(0603mm)_491:3"
  other  "RES-0201(0603mm)_491:4"
  other  "RES-0201(0603mm)_493:1"
  other  "RES-0201(0603mm)_493:2"
  other  "RES-0201(0603mm)_493:3"
  other  "RES-0201(0603mm)_493:4"
  other  "RES-0201(0603mm)_495:1"
  other  "RES-0201(0603mm)_495:2"
  other  "RES-0201(0603mm)_495:3"
  other  "RES-0201(0603mm)_495:4"
  other  "RES-0201(0603mm)_497:1"
  other  "RES-0201(0603mm)_497:2"
  other  "RES-0201(0603mm)_497:3"
  other  "RES-0201(0603mm)_497:4"
  other  "RES-0201(0603mm)_499:1"
  other  "RES-0201(0603mm)_499:2"
  other  "RES-0201(0603mm)_499:3"
  other  "RES-0201(0603mm)_499:4"
  other  "RES-0201(0603mm)_501:1"
  other  "RES-0201(0603mm)_501:2"
  other  "RES-0201(0603mm)_501:3"
  other  "RES-0201(0603mm)_501:4"
  other  "RES-0201(0603mm)_503:1"
  other  "RES-0201(0603mm)_503:2"
  other  "RES-0201(0603mm)_503:3"
  other  "RES-0201(0603mm)_503:4"
  other  "RES-0201(0603mm)_505:1"
  other  "RES-0201(0603mm)_505:2"
  other  "RES-0201(0603mm)_505:3"
  other  "RES-0201(0603mm)_505:4"
  other  "RES-0201(0603mm)_507:1"
  other  "RES-0201(0603mm)_507:2"
  other  "RES-0201(0603mm)_507:3"
  other  "RES-0201(0603mm)_507:4"
  other  "RES-0201(0603mm)_509:1"
  other  "RES-0201(0603mm)_509:2"
  other  "RES-0201(0603mm)_509:3"
  other  "RES-0201(0603mm)_509:4"
  other  "RES-0201(0603mm)_511:1"
  other  "RES-0201(0603mm)_511:2"
  other  "RES-0201(0603mm)_511:3"
  other  "RES-0201(0603mm)_511:4"
  other  "RES-0201(0603mm)_513:1"
  other  "RES-0201(0603mm)_513:2"
  other  "RES-0201(0603mm)_513:3"
  other  "RES-0201(0603mm)_513:4"
  other  "RES-0201(0603mm)_515:1"
  other  "RES-0201(0603mm)_515:2"
  other  "RES-0201(0603mm)_515:3"
  other  "RES-0201(0603mm)_515:4"
  other  "RES-0201(0603mm)_517:1"
  other  "RES-0201(0603mm)_517:2"
  other  "RES-0201(0603mm)_517:3"
  other  "RES-0201(0603mm)_517:4"
  other  "RES-0201(0603mm)_519:1"
  other  "RES-0201(0603mm)_519:2"
  other  "RES-0201(0603mm)_519:3"
  other  "RES-0201(0603mm)_519:4"
  other  "RES-0201(0603mm)_521:1"
  other  "RES-0201(0603mm)_521:2"
  other  "RES-0201(0603mm)_521:3"
  other  "RES-0201(0603mm)_521:4"
  other  "RES-0201(0603mm)_523:1"
  other  "RES-0201(0603mm)_523:2"
  other  "RES-0201(0603mm)_523:3"
  other  "RES-0201(0603mm)_523:4"
  other  "RES-0201(0603mm)_525:1"
  other  "RES-0201(0603mm)_525:2"
  other  "RES-0201(0603mm)_525:3"
  other  "RES-0201(0603mm)_525:4"
  other  "RES-0201(0603mm)_527:1"
  other  "RES-0201(0603mm)_527:2"
  other  "RES-0201(0603mm)_527:3"
  other  "RES-0201(0603mm)_527:4"
  other  "RES-0201(0603mm)_529:1"
  other  "RES-0201(0603mm)_529:2"
  other  "RES-0201(0603mm)_529:3"
  other  "RES-0201(0603mm)_529:4"
  other  "RES-0201(0603mm)_531:1"
  other  "RES-0201(0603mm)_531:2"
  other  "RES-0201(0603mm)_531:3"
  other  "RES-0201(0603mm)_531:4"
  other  "RES-0201(0603mm)_533:1"
  other  "RES-0201(0603mm)_533:2"
  other  "RES-0201(0603mm)_533:3"
  other  "RES-0201(0603mm)_533:4"
  other  "RES-0201(0603mm)_535:1"
  other  "RES-0201(0603mm)_535:2"
  other  "RES-0201(0603mm)_535:3"
  other  "RES-0201(0603mm)_535:4"
  other  "RES-0201(0603mm)_537:1"
  other  "RES-0201(0603mm)_537:2"
  other  "RES-0201(0603mm)_537:3"
  other  "RES-0201(0603mm)_537:4"
  other  "RES-0201(0603mm)_539:1"
  other  "RES-0201(0603mm)_539:2"
  other  "RES-0201(0603mm)_539:3"
  other  "RES-0201(0603mm)_539:4"
  other  "RES-0201(0603mm)_541:1"
  other  "RES-0201(0603mm)_541:2"
  other  "RES-0201(0603mm)_541:3"
  other  "RES-0201(0603mm)_541:4"
  other  "RES-0201(0603mm)_543:1"
  other  "RES-0201(0603mm)_543:2"
  other  "RES-0201(0603mm)_543:3"
  other  "RES-0201(0603mm)_543:4"
  other  "RES-0201(0603mm)_545:1"
  other  "RES-0201(0603mm)_545:2"
  other  "RES-0201(0603mm)_545:3"
  other  "RES-0201(0603mm)_545:4"
  other  "RES-0201(0603mm)_547:1"
  other  "RES-0201(0603mm)_547:2"
  other  "RES-0201(0603mm)_547:3"
  other  "RES-0201(0603mm)_547:4"
  other  "RES-0201(0603mm)_549:1"
  other  "RES-0201(0603mm)_549:2"
  other  "RES-0201(0603mm)_549:3"
  other  "RES-0201(0603mm)_549:4"
  other  "RES-0201(0603mm)_551:1"
  other  "RES-0201(0603mm)_551:2"
  other  "RES-0201(0603mm)_551:3"
  other  "RES-0201(0603mm)_551:4"
  other  "RES-0201(0603mm)_553:1"
  other  "RES-0201(0603mm)_553:2"
  other  "RES-0201(0603mm)_553:3"
  other  "RES-0201(0603mm)_553:4"
  other  "RES-0201(0603mm)_555:1"
  other  "RES-0201(0603mm)_555:2"
  other  "RES-0201(0603mm)_555:3"
  other  "RES-0201(0603mm)_555:4"
  other  "RES-0201(0603mm)_557:1"
  other  "RES-0201(0603mm)_557:2"
  other  "RES-0201(0603mm)_557:3"
  other  "RES-0201(0603mm)_557:4"
  other  "RES-0201(0603mm)_559:1"
  other  "RES-0201(0603mm)_559:2"
  other  "RES-0201(0603mm)_559:3"
  other  "RES-0201(0603mm)_559:4"
  other  "RES-0201(0603mm)_561:1"
  other  "RES-0201(0603mm)_561:2"
  other  "RES-0201(0603mm)_561:3"
  other  "RES-0201(0603mm)_561:4"
  other  "RES-0201(0603mm)_563:1"
  other  "RES-0201(0603mm)_563:2"
  other  "RES-0201(0603mm)_563:3"
  other  "RES-0201(0603mm)_563:4"
  other  "RES-0201(0603mm)_565:1"
  other  "RES-0201(0603mm)_565:2"
  other  "RES-0201(0603mm)_565:3"
  other  "RES-0201(0603mm)_565:4"
  other  "RES-0201(0603mm)_567:1"
  other  "RES-0201(0603mm)_567:2"
  other  "RES-0201(0603mm)_567:3"
  other  "RES-0201(0603mm)_567:4"
  other  "RES-0201(0603mm)_569:1"
  other  "RES-0201(0603mm)_569:2"
  other  "RES-0201(0603mm)_569:3"
  other  "RES-0201(0603mm)_569:4"
  other  "RES-0201(0603mm)_571:1"
  other  "RES-0201(0603mm)_571:2"
  other  "RES-0201(0603mm)_571:3"
  other  "RES-0201(0603mm)_571:4"
  other  "RES-0201(0603mm)_573:1"
  other  "RES-0201(0603mm)_573:2"
  other  "RES-0201(0603mm)_573:3"
  other  "RES-0201(0603mm)_573:4"
  other  "RES-0201(0603mm)_575:1"
  other  "RES-0201(0603mm)_575:2"
  other  "RES-0201(0603mm)_575:3"
  other  "RES-0201(0603mm)_575:4"
  other  "RES-0201(0603mm)_577:1"
  other  "RES-0201(0603mm)_577:2"
  other  "RES-0201(0603mm)_577:3"
  other  "RES-0201(0603mm)_577:4"
  other  "RES-0201(0603mm)_579:1"
  other  "RES-0201(0603mm)_579:2"
  other  "RES-0201(0603mm)_579:3"
  other  "RES-0201(0603mm)_579:4"
  other  "RES-0201(0603mm)_581:1"
  other  "RES-0201(0603mm)_581:2"
  other  "RES-0201(0603mm)_581:3"
  other  "RES-0201(0603mm)_581:4"
  other  "RES-0201(0603mm)_583:1"
  other  "RES-0201(0603mm)_583:2"
  other  "RES-0201(0603mm)_583:3"
  other  "RES-0201(0603mm)_583:4"
  other  "RES-0201(0603mm)_585:1"
  other  "RES-0201(0603mm)_585:2"
  other  "RES-0201(0603mm)_585:3"
  other  "RES-0201(0603mm)_585:4"
  other  "RES-0201(0603mm)_587:1"
  other  "RES-0201(0603mm)_587:2"
  other  "RES-0201(0603mm)_587:3"
  other  "RES-0201(0603mm)_587:4"
  other  "RES-0201(0603mm)_589:1"
  other  "RES-0201(0603mm)_589:2"
  other  "RES-0201(0603mm)_589:3"
  other  "RES-0201(0603mm)_589:4"
  other  "RES-0201(0603mm)_591:1"
  other  "RES-0201(0603mm)_591:2"
  other  "RES-0201(0603mm)_591:3"
  other  "RES-0201(0603mm)_591:4"
  other  "RES-0201(0603mm)_593:1"
  other  "RES-0201(0603mm)_593:2"
  other  "RES-0201(0603mm)_593:3"
  other  "RES-0201(0603mm)_593:4"
  other  "RES-0201(0603mm)_595:1"
  other  "RES-0201(0603mm)_595:2"
  other  "RES-0201(0603mm)_595:3"
  other  "RES-0201(0603mm)_595:4"
  other  "RES-0201(0603mm)_597:1"
  other  "RES-0201(0603mm)_597:2"
  other  "RES-0201(0603mm)_597:3"
  other  "RES-0201(0603mm)_597:4"
  other  "RES-0402(1005mm)_599:1"
  other  "RES-0402(1005mm)_599:2"
  other  "RES-0402(1005mm)_599:3"
  other  "RES-0402(1005mm)_599:4"
  other  "RES-0201(0603mm)_601:1"
  other  "RES-0201(0603mm)_601:2"
  other  "RES-0201(0603mm)_601:3"
  other  "RES-0201(0603mm)_601:4"
  other  "RES-0201(0603mm)_603:1"
  other  "RES-0201(0603mm)_603:2"
  other  "RES-0201(0603mm)_603:3"
  other  "RES-0201(0603mm)_603:4"
  other  "RES-0402(1005mm)_605:1"
  other  "RES-0402(1005mm)_605:2"
  other  "RES-0402(1005mm)_605:3"
  other  "RES-0402(1005mm)_605:4"
  other  "RES-0402(1005mm)_607:1"
  other  "RES-0402(1005mm)_607:2"
  other  "RES-0402(1005mm)_607:3"
  other  "RES-0402(1005mm)_607:4"
  other  "RES-0201(0603mm)_609:1"
  other  "RES-0201(0603mm)_609:2"
  other  "RES-0201(0603mm)_609:3"
  other  "RES-0201(0603mm)_609:4"
  other  "RES-0201(0603mm)_611:1"
  other  "RES-0201(0603mm)_611:2"
  other  "RES-0201(0603mm)_611:3"
  other  "RES-0201(0603mm)_611:4"
  other  "RES-0201(0603mm)_613:1"
  other  "RES-0201(0603mm)_613:2"
  other  "RES-0201(0603mm)_613:3"
  other  "RES-0201(0603mm)_613:4"
  other  "RES-0201(0603mm)_615:1"
  other  "RES-0201(0603mm)_615:2"
  other  "RES-0201(0603mm)_615:3"
  other  "RES-0201(0603mm)_615:4"
  other  "RES-0201(0603mm)_617:1"
  other  "RES-0201(0603mm)_617:2"
  other  "RES-0201(0603mm)_617:3"
  other  "RES-0201(0603mm)_617:4"
  other  "RES-0201(0603mm)_619:1"
  other  "RES-0201(0603mm)_619:2"
  other  "RES-0201(0603mm)_619:3"
  other  "RES-0201(0603mm)_619:4"
  other  "RES-0201(0603mm)_621:1"
  other  "RES-0201(0603mm)_621:2"
  other  "RES-0201(0603mm)_621:3"
  other  "RES-0201(0603mm)_621:4"
  other  "RES-0201(0603mm)_623:1"
  other  "RES-0201(0603mm)_623:2"
  other  "RES-0201(0603mm)_623:3"
  other  "RES-0201(0603mm)_623:4"
  other  "RES-0201(0603mm)_625:1"
  other  "RES-0201(0603mm)_625:2"
  other  "RES-0201(0603mm)_625:3"
  other  "RES-0201(0603mm)_625:4"
  other  "RES-0201(0603mm)_627:1"
  other  "RES-0201(0603mm)_627:2"
  other  "RES-0201(0603mm)_627:3"
  other  "RES-0201(0603mm)_627:4"
  other  "RES-0201(0603mm)_629:1"
  other  "RES-0201(0603mm)_629:2"
  other  "RES-0201(0603mm)_629:3"
  other  "RES-0201(0603mm)_629:4"
  other  "RES-0201(0603mm)_631:1"
  other  "RES-0201(0603mm)_631:2"
  other  "RES-0201(0603mm)_631:3"
  other  "RES-0201(0603mm)_631:4"
  other  "RES-0201(0603mm)_633:1"
  other  "RES-0201(0603mm)_633:2"
  other  "RES-0201(0603mm)_633:3"
  other  "RES-0201(0603mm)_633:4"
  other  "RES-0201(0603mm)_635:1"
  other  "RES-0201(0603mm)_635:2"
  other  "RES-0201(0603mm)_635:3"
  other  "RES-0201(0603mm)_635:4"
  other  "RES-0201(0603mm)_637:1"
  other  "RES-0201(0603mm)_637:2"
  other  "RES-0201(0603mm)_637:3"
  other  "RES-0201(0603mm)_637:4"
  other  "User_Library-SOT-23-3-1_SOT-23-3_Body_639:1"
  other  "User_Library-SOT-23-3-1_SOT-23-3_Foot_640:1"
  other  "User_Library-SOT-23-3-1_SOT-23-3_Foot_641:1"
  other  "User_Library-SOT-23-3-1_SOT-23-3_Foot_642:1"
  other  "User_Library-SOT-23-3-1_SOT-23-3_Body_639:2"
  other  "User_Library-SOT-23-3-1_SOT-23-3_Foot_640:2"
  other  "User_Library-SOT-23-3-1_SOT-23-3_Foot_641:2"
  other  "User_Library-SOT-23-3-1_SOT-23-3_Foot_642:2"
  other  "User_Library-SOT-23-3-1_SOT-23-3_Body_639:3"
  other  "User_Library-SOT-23-3-1_SOT-23-3_Foot_640:3"
  other  "User_Library-SOT-23-3-1_SOT-23-3_Foot_641:3"
  other  "User_Library-SOT-23-3-1_SOT-23-3_Foot_642:3"
  other  "User_Library-SOT-23-3-1_SOT-23-3_Body_639:4"
  other  "User_Library-SOT-23-3-1_SOT-23-3_Foot_640:4"
  other  "User_Library-SOT-23-3-1_SOT-23-3_Foot_641:4"
  other  "User_Library-SOT-23-3-1_SOT-23-3_Foot_642:4"
  other  "User_Library-SOT-563_651:1"
  other  "User_Library-SOT-563_653:1"
  other  "User_Library-SOT-563_655:1"
  other  "User_Library-SOT-563_657:1"
  other  "User_Library-SOT-23-3-1_SOT-23-3_Body_639:5"
  other  "User_Library-SOT-23-3-1_SOT-23-3_Foot_640:5"
  other  "User_Library-SOT-23-3-1_SOT-23-3_Foot_641:5"
  other  "User_Library-SOT-23-3-1_SOT-23-3_Foot_642:5"
  other  "User_Library-SOT-23-3-1_SOT-23-3_Body_639:6"
  other  "User_Library-SOT-23-3-1_SOT-23-3_Foot_640:6"
  other  "User_Library-SOT-23-3-1_SOT-23-3_Foot_641:6"
  other  "User_Library-SOT-23-3-1_SOT-23-3_Foot_642:6"
  other  "SRP5030CA_663:1"
  other  "SRP5030CA_663:2"
  other  "SRP5030CA_663:3"
  other  "SRP4020FA_665:1"
  other  "SRP4020FA_665:2"
  other  "SRN2512_series_667:1"
  other  "SRN2512_series_667:2"
  other  "SRN2512_series_667:3"
  other  "SRN2512_series_667:4"
  other  "SRN2512_series_669:1"
  other  "SRN2512_series_669:2"
  other  "SRN2512_series_669:3"
  other  "SRN2512_series_669:4"
  other  "SRN2512_series_671:1"
  other  "SRN2512_series_671:2"
  other  "SRN2512_series_671:3"
  other  "SRN2512_series_671:4"
  other  "SRP4020FA_673:1"
  other  "SRP4020FA_673:2"
  other  "SRN2512_series_675:1"
  other  "SRN2512_series_675:2"
  other  "SRN2512_series_675:3"
  other  "SRN2512_series_675:4"
  other  "SRN2512_series_677:1"
  other  "SRN2512_series_677:2"
  other  "SRN2512_series_677:3"
  other  "SRN2512_series_677:4"
  other  "SRN2512_series_679:1"
  other  "SRN2512_series_679:2"
  other  "SRN2512_series_679:3"
  other  "SRN2512_series_679:4"
  other  "RES-0201(0603mm)_681:1"
  other  "RES-0201(0603mm)_681:2"
  other  "RES-0201(0603mm)_681:3"
  other  "RES-0201(0603mm)_681:4"
  other  "RES-0402(1005mm)_683:1"
  other  "RES-0402(1005mm)_683:2"
  other  "RES-0402(1005mm)_683:3"
  other  "RES-0402(1005mm)_683:4"
  other  "User_Library-Header_Male_2Pin_PinArray_685:1"
  other  "User_Library-Header_Male_2Pin_PinArray_685:2"
  other  "User_Library-Header_Male_2Pin_BodyArray_686:1"
  other  "User_Library-Header_Male_2Pin_BodyArray_686:2"
  other  "85r4853_1932258-1_689:1"
  other  "85r4853_1932258-1_691:1"
  other  "_MMT-108-01-T-SH-LC_pins_693:1"
  other  "_MMT-108-01-T-SH-LC_body_694:1"
  other  "c-2201778-1-a-3d_697:1"
  other  "_MMT-104-01-T-SH-LC_pins_699:1"
  other  "_MMT-104-01-T-SH-LC_body_700:1"
  extrude  "Extruded_703:1"  [1 undecoded]
  other  "WE-VS_0603_VS_706:1"
  other  "WE-VS_0603_VS_708:1"
  other  "WE-VS_0603_VS_710:1"
  other  "WE-VS_0603_VS_712:1"
  other  "WE-VS_0603_VS_714:1"
  other  "WE-VS_0603_VS_716:1"
  extrude  "Extruded_718:1"  [1 undecoded]
  other  "User_Library-sq3427eev-t1-ge3_721:1"
  extrude  "Extruded_718:2"  [1 undecoded]
  other  "User_Library-LTST-C190GKT_Pad005_725:1"
  other  "User_Library-LTST-C190GKT_Pad001_726:1"
  other  "User_Library-LTST-C190GKT_Pad001_726:2"
  other  "User_Library-LTST-C190GKT_Pad004_727:1"
  other  "User_Library-LTST-C190GKT_Pad003_728:1"
  other  "User_Library-LTST-C190GKT_Pad003_728:2"
  other  "User_Library-LTST-C190GKT_Lens_729:1"
  other  "User_Library-LTST-C190GKT_Pad_730:1"
  other  "User_Library-DO-214AA(SMB)_733:1"
  other  "User_Library-led0603_YEL_735:1"
  other  "User_Library-led0603_YEL_735:2"
  other  "User_Library-led0603_YEL_735:3"
  other  "User_Library-led0603_YEL_735:4"
  other  "User_Library-led0603_YEL_735:5"
  other  "User_Library-led0603_YEL_735:6"
  other  "User_Library-led0603_YEL_735:7"
  other  "User_Library-SOD-123_DiodesInc_737:1"
  other  "User_Library-LTST-C190GKT_Pad005_725:2"
  other  "User_Library-LTST-C190GKT_Pad001_726:3"
  other  "User_Library-LTST-C190GKT_Pad001_726:4"
  other  "User_Library-LTST-C190GKT_Pad004_727:2"
  other  "User_Library-LTST-C190GKT_Pad003_728:3"
  other  "User_Library-LTST-C190GKT_Pad003_728:4"
  other  "User_Library-LTST-C190GKT_Lens_729:2"
  other  "User_Library-LTST-C190GKT_Pad_730:2"
  other  "User_Library-LTST-C190GKT_Pad005_725:3"
  other  "User_Library-LTST-C190GKT_Pad001_726:5"
  other  "User_Library-LTST-C190GKT_Pad001_726:6"
  other  "User_Library-LTST-C190GKT_Pad004_727:3"
  other  "User_Library-LTST-C190GKT_Pad003_728:5"
  other  "User_Library-LTST-C190GKT_Pad003_728:6"
  other  "User_Library-LTST-C190GKT_Lens_729:3"
  other  "User_Library-LTST-C190GKT_Pad_730:3"
  other  "User_Library-LTST-C190EKT_Pad_743:1"
  other  "User_Library-LTST-C190EKT_Pad005_744:1"
  other  "User_Library-LTST-C190EKT_Pad001_745:1"
  other  "User_Library-LTST-C190EKT_Pad001_745:2"
  other  "User_Library-LTST-C190EKT_Pad004_746:1"
  other  "User_Library-LTST-C190EKT_Pad003_747:1"
  other  "User_Library-LTST-C190EKT_Pad003_747:2"
  other  "User_Library-LTST-C190EKT_Lens_748:1"
  other  "User_Library-LTST-C190GKT_Pad005_725:4"
  other  "User_Library-LTST-C190GKT_Pad001_726:7"
  other  "User_Library-LTST-C190GKT_Pad001_726:8"
  other  "User_Library-LTST-C190GKT_Pad004_727:4"
  other  "User_Library-LTST-C190GKT_Pad003_728:7"
  other  "User_Library-LTST-C190GKT_Pad003_728:8"
  other  "User_Library-LTST-C190GKT_Lens_729:4"
  other  "User_Library-LTST-C190GKT_Pad_730:4"
  other  "User_Library-LTST-C190GKT_Pad005_725:5"
  other  "User_Library-LTST-C190GKT_Pad001_726:9"
  other  "User_Library-LTST-C190GKT_Pad001_726:10"
  other  "User_Library-LTST-C190GKT_Pad004_727:5"
  other  "User_Library-LTST-C190GKT_Pad003_728:9"
  other  "User_Library-LTST-C190GKT_Pad003_728:10"
  other  "User_Library-LTST-C190GKT_Lens_729:5"
  other  "User_Library-LTST-C190GKT_Pad_730:5"
  other  "User_Library-LTST-C190GKT_Pad005_725:6"
  other  "User_Library-LTST-C190GKT_Pad001_726:11"
  other  "User_Library-LTST-C190GKT_Pad001_726:12"
  other  "User_Library-LTST-C190GKT_Pad004_727:6"
  other  "User_Library-LTST-C190GKT_Pad003_728:11"
  other  "User_Library-LTST-C190GKT_Pad003_728:12"
  other  "User_Library-LTST-C190GKT_Lens_729:6"
  other  "User_Library-LTST-C190GKT_Pad_730:6"
  other  "User_Library-LTST-C190TBKT_Pad_78:2"
  other  "User_Library-LTST-C190TBKT_Pad005_79:2"
  other  "User_Library-LTST-C190TBKT_Pad001_80:3"
  other  "User_Library-LTST-C190TBKT_Pad001_80:4"
  other  "User_Library-LTST-C190TBKT_Pad004_81:2"
  other  "User_Library-LTST-C190TBKT_Pad003_82:3"
  other  "User_Library-LTST-C190TBKT_Pad003_82:4"
  other  "User_Library-LTST-C190TBKT_Lens_83:2"
  other  "User_Library-0603(1608M)_Cap_759:1"
  other  "User_Library-0603(1608M)_Cap_759:2"
  other  "User_Library-0603(1608M)_Cap_759:3"
  other  "User_Library-0402(1005M)_Cap_761:1"
  other  "User_Library-0402(1005M)_Cap_761:2"
  other  "User_Library-0402(1005M)_Cap_761:3"
  other  "User_Library-0402(1005M)_Cap_763:1"
  other  "User_Library-0402(1005M)_Cap_763:2"
  other  "User_Library-0402(1005M)_Cap_763:3"
  other  "User_Library-0402(1005M)_Cap_765:1"
  other  "User_Library-0402(1005M)_Cap_765:2"
  other  "User_Library-0402(1005M)_Cap_765:3"
  other  "User_Library-0201(0603M)_Cap_767:1"
  other  "User_Library-0201(0603M)_Cap_767:2"
  other  "User_Library-0201(0603M)_Cap_767:3"
  other  "User_Library-0805_SMD_Capacitor_769:1"
  other  "User_Library-0805_SMD_Capacitor_771:1"
  other  "User_Library-0805_SMD_Capacitor_773:1"
  other  "User_Library-0201(0603M)_Cap_775:1"
  other  "User_Library-0201(0603M)_Cap_775:2"
  other  "User_Library-0201(0603M)_Cap_775:3"
  other  "User_Library-0201(0603M)_Cap_777:1"
  other  "User_Library-0201(0603M)_Cap_777:2"
  other  "User_Library-0201(0603M)_Cap_777:3"
  other  "User_Library-0402(1005M)_Cap_779:1"
  other  "User_Library-0402(1005M)_Cap_779:2"
  other  "User_Library-0402(1005M)_Cap_779:3"
  other  "User_Library-0402(1005M)_Cap_781:1"
  other  "User_Library-0402(1005M)_Cap_781:2"
  other  "User_Library-0402(1005M)_Cap_781:3"
  other  "User_Library-0201(0603M)_Cap_783:1"
  other  "User_Library-0201(0603M)_Cap_783:2"
  other  "User_Library-0201(0603M)_Cap_783:3"
  other  "User_Library-1206_SMD_Capacitor_785:1"
  other  "User_Library-1206_SMD_Capacitor_787:1"
  other  "User_Library-1206_SMD_Capacitor_789:1"
  other  "User_Library-1206_SMD_Capacitor_791:1"
  other  "User_Library-0201(0603M)_Cap_793:1"
  other  "User_Library-0201(0603M)_Cap_793:2"
  other  "User_Library-0201(0603M)_Cap_793:3"
  other  "User_Library-0201(0603M)_Cap_795:1"
  other  "User_Library-0201(0603M)_Cap_795:2"
  other  "User_Library-0201(0603M)_Cap_795:3"
  other  "User_Library-0201(0603M)_Cap_797:1"
  other  "User_Library-0201(0603M)_Cap_797:2"
  other  "User_Library-0201(0603M)_Cap_797:3"
  other  "User_Library-0402(1005M)_Cap_799:1"
  other  "User_Library-0402(1005M)_Cap_799:2"
  other  "User_Library-0402(1005M)_Cap_799:3"
  other  "User_Library-0201(0603M)_Cap_801:1"
  other  "User_Library-0201(0603M)_Cap_801:2"
  other  "User_Library-0201(0603M)_Cap_801:3"
  other  "User_Library-0603(1608M)_Cap_803:1"
  other  "User_Library-0603(1608M)_Cap_803:2"
  other  "User_Library-0603(1608M)_Cap_803:3"
  other  "User_Library-0402(1005M)_Cap_805:1"
  other  "User_Library-0402(1005M)_Cap_805:2"
  other  "User_Library-0402(1005M)_Cap_805:3"
  other  "User_Library-0201(0603M)_Cap_807:1"
  other  "User_Library-0201(0603M)_Cap_807:2"
  other  "User_Library-0201(0603M)_Cap_807:3"
  other  "User_Library-0201(0603M)_Cap_809:1"
  other  "User_Library-0201(0603M)_Cap_809:2"
  other  "User_Library-0201(0603M)_Cap_809:3"
  other  "User_Library-0402(1005M)_Cap_811:1"
  other  "User_Library-0402(1005M)_Cap_811:2"
  other  "User_Library-0402(1005M)_Cap_811:3"
  other  "User_Library-0402(1005M)_Cap_813:1"
  other  "User_Library-0402(1005M)_Cap_813:2"
  other  "User_Library-0402(1005M)_Cap_813:3"
  other  "User_Library-0201(0603M)_Cap_815:1"
  other  "User_Library-0201(0603M)_Cap_815:2"
  other  "User_Library-0201(0603M)_Cap_815:3"
  other  "User_Library-0201(0603M)_Cap_817:1"
  other  "User_Library-0201(0603M)_Cap_817:2"
  other  "User_Library-0201(0603M)_Cap_817:3"
  other  "User_Library-0201(0603M)_Cap_819:1"
  other  "User_Library-0201(0603M)_Cap_819:2"
  other  "User_Library-0201(0603M)_Cap_819:3"
  other  "User_Library-0201(0603M)_Cap_821:1"
  other  "User_Library-0201(0603M)_Cap_821:2"
  other  "User_Library-0201(0603M)_Cap_821:3"
  other  "User_Library-0201(0603M)_Cap_823:1"
  other  "User_Library-0201(0603M)_Cap_823:2"
  other  "User_Library-0201(0603M)_Cap_823:3"
  other  "User_Library-0201(0603M)_Cap_825:1"
  other  "User_Library-0201(0603M)_Cap_825:2"
  other  "User_Library-0201(0603M)_Cap_825:3"
  other  "User_Library-0201(0603M)_Cap_827:1"
  other  "User_Library-0201(0603M)_Cap_827:2"
  other  "User_Library-0201(0603M)_Cap_827:3"
  other  "User_Library-0201(0603M)_Cap_829:1"
  other  "User_Library-0201(0603M)_Cap_829:2"
  other  "User_Library-0201(0603M)_Cap_829:3"
  other  "User_Library-AVX_BCASE_831:1"
  other  "User_Library-0201(0603M)_Cap_833:1"
  other  "User_Library-0201(0603M)_Cap_833:2"
  other  "User_Library-0201(0603M)_Cap_833:3"
  other  "User_Library-0201(0603M)_Cap_835:1"
  other  "User_Library-0201(0603M)_Cap_835:2"
  other  "User_Library-0201(0603M)_Cap_835:3"
  other  "User_Library-0201(0603M)_Cap_837:1"
  other  "User_Library-0201(0603M)_Cap_837:2"
  other  "User_Library-0201(0603M)_Cap_837:3"
  other  "User_Library-0201(0603M)_Cap_839:1"
  other  "User_Library-0201(0603M)_Cap_839:2"
  other  "User_Library-0201(0603M)_Cap_839:3"
  other  "User_Library-0201(0603M)_Cap_841:1"
  other  "User_Library-0201(0603M)_Cap_841:2"
  other  "User_Library-0201(0603M)_Cap_841:3"
  other  "User_Library-0201(0603M)_Cap_843:1"
  other  "User_Library-0201(0603M)_Cap_843:2"
  other  "User_Library-0201(0603M)_Cap_843:3"
  other  "User_Library-0201(0603M)_Cap_845:1"
  other  "User_Library-0201(0603M)_Cap_845:2"
  other  "User_Library-0201(0603M)_Cap_845:3"
  other  "User_Library-0201(0603M)_Cap_847:1"
  other  "User_Library-0201(0603M)_Cap_847:2"
  other  "User_Library-0201(0603M)_Cap_847:3"
  other  "User_Library-0201(0603M)_Cap_849:1"
  other  "User_Library-0201(0603M)_Cap_849:2"
  other  "User_Library-0201(0603M)_Cap_849:3"
  other  "User_Library-0201(0603M)_Cap_851:1"
  other  "User_Library-0201(0603M)_Cap_851:2"
  other  "User_Library-0201(0603M)_Cap_851:3"
  other  "User_Library-0201(0603M)_Cap_853:1"
  other  "User_Library-0201(0603M)_Cap_853:2"
  other  "User_Library-0201(0603M)_Cap_853:3"
  other  "User_Library-0201(0603M)_Cap_855:1"
  other  "User_Library-0201(0603M)_Cap_855:2"
  other  "User_Library-0201(0603M)_Cap_855:3"
  other  "User_Library-0201(0603M)_Cap_857:1"
  other  "User_Library-0201(0603M)_Cap_857:2"
  other  "User_Library-0201(0603M)_Cap_857:3"
  other  "User_Library-0201(0603M)_Cap_859:1"
  other  "User_Library-0201(0603M)_Cap_859:2"
  other  "User_Library-0201(0603M)_Cap_859:3"
  other  "User_Library-AVX_BCASE_861:1"
  other  "User_Library-0201(0603M)_Cap_863:1"
  other  "User_Library-0201(0603M)_Cap_863:2"
  other  "User_Library-0201(0603M)_Cap_863:3"
  other  "User_Library-0201(0603M)_Cap_865:1"
  other  "User_Library-0201(0603M)_Cap_865:2"
  other  "User_Library-0201(0603M)_Cap_865:3"
  other  "User_Library-0201(0603M)_Cap_867:1"
  other  "User_Library-0201(0603M)_Cap_867:2"
  other  "User_Library-0201(0603M)_Cap_867:3"
  other  "User_Library-0201(0603M)_Cap_869:1"
  other  "User_Library-0201(0603M)_Cap_869:2"
  other  "User_Library-0201(0603M)_Cap_869:3"
  other  "User_Library-0201(0603M)_Cap_871:1"
  other  "User_Library-0201(0603M)_Cap_871:2"
  other  "User_Library-0201(0603M)_Cap_871:3"
  other  "User_Library-0201(0603M)_Cap_873:1"
  other  "User_Library-0201(0603M)_Cap_873:2"
  other  "User_Library-0201(0603M)_Cap_873:3"
  other  "User_Library-0201(0603M)_Cap_875:1"
  other  "User_Library-0201(0603M)_Cap_875:2"
  other  "User_Library-0201(0603M)_Cap_875:3"
  other  "User_Library-0201(0603M)_Cap_877:1"
  other  "User_Library-0201(0603M)_Cap_877:2"
  other  "User_Library-0201(0603M)_Cap_877:3"
  other  "User_Library-0201(0603M)_Cap_879:1"
  other  "User_Library-0201(0603M)_Cap_879:2"
  other  "User_Library-0201(0603M)_Cap_879:3"
  other  "User_Library-0201(0603M)_Cap_881:1"
  other  "User_Library-0201(0603M)_Cap_881:2"
  other  "User_Library-0201(0603M)_Cap_881:3"
  other  "User_Library-0201(0603M)_Cap_883:1"
  other  "User_Library-0201(0603M)_Cap_883:2"
  other  "User_Library-0201(0603M)_Cap_883:3"
  other  "User_Library-0201(0603M)_Cap_885:1"
  other  "User_Library-0201(0603M)_Cap_885:2"
  other  "User_Library-0201(0603M)_Cap_885:3"
  other  "User_Library-0201(0603M)_Cap_887:1"
  other  "User_Library-0201(0603M)_Cap_887:2"
  other  "User_Library-0201(0603M)_Cap_887:3"
  other  "User_Library-0201(0603M)_Cap_889:1"
  other  "User_Library-0201(0603M)_Cap_889:2"
  other  "User_Library-0201(0603M)_Cap_889:3"
  other  "User_Library-0201(0603M)_Cap_891:1"
  other  "User_Library-0201(0603M)_Cap_891:2"
  other  "User_Library-0201(0603M)_Cap_891:3"
  other  "User_Library-0201(0603M)_Cap_893:1"
  other  "User_Library-0201(0603M)_Cap_893:2"
  other  "User_Library-0201(0603M)_Cap_893:3"
  other  "User_Library-0201(0603M)_Cap_895:1"
  other  "User_Library-0201(0603M)_Cap_895:2"
  other  "User_Library-0201(0603M)_Cap_895:3"
  other  "User_Library-0201(0603M)_Cap_897:1"
  other  "User_Library-0201(0603M)_Cap_897:2"
  other  "User_Library-0201(0603M)_Cap_897:3"
  other  "User_Library-1206_SMD_Capacitor_899:1"
  other  "User_Library-0201(0603M)_Cap_901:1"
  other  "User_Library-0201(0603M)_Cap_901:2"
  other  "User_Library-0201(0603M)_Cap_901:3"
  other  "User_Library-0201(0603M)_Cap_903:1"
  other  "User_Library-0201(0603M)_Cap_903:2"
  other  "User_Library-0201(0603M)_Cap_903:3"
  other  "User_Library-0201(0603M)_Cap_905:1"
  other  "User_Library-0201(0603M)_Cap_905:2"
  other  "User_Library-0201(0603M)_Cap_905:3"
  other  "User_Library-0201(0603M)_Cap_907:1"
  other  "User_Library-0201(0603M)_Cap_907:2"
  other  "User_Library-0201(0603M)_Cap_907:3"
  other  "User_Library-0201(0603M)_Cap_909:1"
  other  "User_Library-0201(0603M)_Cap_909:2"
  other  "User_Library-0201(0603M)_Cap_909:3"
  other  "User_Library-0201(0603M)_Cap_911:1"
  other  "User_Library-0201(0603M)_Cap_911:2"
  other  "User_Library-0201(0603M)_Cap_911:3"
  other  "User_Library-0201(0603M)_Cap_913:1"
  other  "User_Library-0201(0603M)_Cap_913:2"
  other  "User_Library-0201(0603M)_Cap_913:3"
  other  "User_Library-0201(0603M)_Cap_915:1"
  other  "User_Library-0201(0603M)_Cap_915:2"
  other  "User_Library-0201(0603M)_Cap_915:3"
  other  "User_Library-0201(0603M)_Cap_917:1"
  other  "User_Library-0201(0603M)_Cap_917:2"
  other  "User_Library-0201(0603M)_Cap_917:3"
  other  "User_Library-0201(0603M)_Cap_919:1"
  other  "User_Library-0201(0603M)_Cap_919:2"
  other  "User_Library-0201(0603M)_Cap_919:3"
  other  "User_Library-0201(0603M)_Cap_921:1"
  other  "User_Library-0201(0603M)_Cap_921:2"
  other  "User_Library-0201(0603M)_Cap_921:3"
  other  "User_Library-0201(0603M)_Cap_923:1"
  other  "User_Library-0201(0603M)_Cap_923:2"
  other  "User_Library-0201(0603M)_Cap_923:3"
  other  "User_Library-0201(0603M)_Cap_925:1"
  other  "User_Library-0201(0603M)_Cap_925:2"
  other  "User_Library-0201(0603M)_Cap_925:3"
  other  "User_Library-0402(1005M)_Cap_927:1"
  other  "User_Library-0402(1005M)_Cap_927:2"
  other  "User_Library-0402(1005M)_Cap_927:3"
  other  "User_Library-0201(0603M)_Cap_929:1"
  other  "User_Library-0201(0603M)_Cap_929:2"
  other  "User_Library-0201(0603M)_Cap_929:3"
  other  "User_Library-0603(1608M)_Cap_931:1"
  other  "User_Library-0603(1608M)_Cap_931:2"
  other  "User_Library-0603(1608M)_Cap_931:3"
  other  "User_Library-0201(0603M)_Cap_933:1"
  other  "User_Library-0201(0603M)_Cap_933:2"
  other  "User_Library-0201(0603M)_Cap_933:3"
  other  "User_Library-0201(0603M)_Cap_935:1"
  other  "User_Library-0201(0603M)_Cap_935:2"
  other  "User_Library-0201(0603M)_Cap_935:3"
  other  "User_Library-0201(0603M)_Cap_937:1"
  other  "User_Library-0201(0603M)_Cap_937:2"
  other  "User_Library-0201(0603M)_Cap_937:3"
  other  "User_Library-0201(0603M)_Cap_939:1"
  other  "User_Library-0201(0603M)_Cap_939:2"
  other  "User_Library-0201(0603M)_Cap_939:3"
  other  "User_Library-0201(0603M)_Cap_941:1"
  other  "User_Library-0201(0603M)_Cap_941:2"
  other  "User_Library-0201(0603M)_Cap_941:3"
  other  "User_Library-0201(0603M)_Cap_943:1"
  other  "User_Library-0201(0603M)_Cap_943:2"
  other  "User_Library-0201(0603M)_Cap_943:3"
  other  "User_Library-0201(0603M)_Cap_945:1"
  other  "User_Library-0201(0603M)_Cap_945:2"
  other  "User_Library-0201(0603M)_Cap_945:3"
  other  "User_Library-0805_SMD_Capacitor_947:1"
  other  "User_Library-1210(3225M)_Cap_949:1"
  other  "User_Library-1210(3225M)_Cap_949:2"
  other  "User_Library-1210(3225M)_Cap_949:3"
  other  "User_Library-0201(0603M)_Cap_951:1"
  other  "User_Library-0201(0603M)_Cap_951:2"
  other  "User_Library-0201(0603M)_Cap_951:3"
  other  "User_Library-0603(1608M)_Cap_953:1"
  other  "User_Library-0603(1608M)_Cap_953:2"
  other  "User_Library-0603(1608M)_Cap_953:3"
  other  "User_Library-0201(0603M)_Cap_955:1"
  other  "User_Library-0201(0603M)_Cap_955:2"
  other  "User_Library-0201(0603M)_Cap_955:3"
  other  "User_Library-0201(0603M)_Cap_957:1"
  other  "User_Library-0201(0603M)_Cap_957:2"
  other  "User_Library-0201(0603M)_Cap_957:3"
  other  "User_Library-1210(3225M)_Cap_959:1"
  other  "User_Library-1210(3225M)_Cap_959:2"
  other  "User_Library-1210(3225M)_Cap_959:3"
  other  "User_Library-0201(0603M)_Cap_961:1"
  other  "User_Library-0201(0603M)_Cap_961:2"
  other  "User_Library-0201(0603M)_Cap_961:3"
  other  "User_Library-0201(0603M)_Cap_963:1"
  other  "User_Library-0201(0603M)_Cap_963:2"
  other  "User_Library-0201(0603M)_Cap_963:3"
  other  "User_Library-0201(0603M)_Cap_965:1"
  other  "User_Library-0201(0603M)_Cap_965:2"
  other  "User_Library-0201(0603M)_Cap_965:3"
  other  "User_Library-0201(0603M)_Cap_967:1"
  other  "User_Library-0201(0603M)_Cap_967:2"
  other  "User_Library-0201(0603M)_Cap_967:3"
  other  "User_Library-0603(1608M)_Cap_969:1"
  other  "User_Library-0603(1608M)_Cap_969:2"
  other  "User_Library-0603(1608M)_Cap_969:3"
  other  "User_Library-1210(3225M)_Cap_971:1"
  other  "User_Library-1210(3225M)_Cap_971:2"
  other  "User_Library-1210(3225M)_Cap_971:3"
  other  "User_Library-0201(0603M)_Cap_973:1"
  other  "User_Library-0201(0603M)_Cap_973:2"
  other  "User_Library-0201(0603M)_Cap_973:3"
  other  "User_Library-0201(0603M)_Cap_975:1"
  other  "User_Library-0201(0603M)_Cap_975:2"
  other  "User_Library-0201(0603M)_Cap_975:3"
  other  "User_Library-0201(0603M)_Cap_977:1"
  other  "User_Library-0201(0603M)_Cap_977:2"
  other  "User_Library-0201(0603M)_Cap_977:3"
  other  "User_Library-0201(0603M)_Cap_979:1"
  other  "User_Library-0201(0603M)_Cap_979:2"
  other  "User_Library-0201(0603M)_Cap_979:3"
  other  "User_Library-0201(0603M)_Cap_981:1"
  other  "User_Library-0201(0603M)_Cap_981:2"
  other  "User_Library-0201(0603M)_Cap_981:3"
  other  "User_Library-0201(0603M)_Cap_983:1"
  other  "User_Library-0201(0603M)_Cap_983:2"
  other  "User_Library-0201(0603M)_Cap_983:3"
  other  "User_Library-0201(0603M)_Cap_985:1"
  other  "User_Library-0201(0603M)_Cap_985:2"
  other  "User_Library-0201(0603M)_Cap_985:3"
  other  "User_Library-0201(0603M)_Cap_987:1"
  other  "User_Library-0201(0603M)_Cap_987:2"
  other  "User_Library-0201(0603M)_Cap_987:3"
  other  "User_Library-0603(1608M)_Cap_989:1"
  other  "User_Library-0603(1608M)_Cap_989:2"
  other  "User_Library-0603(1608M)_Cap_989:3"
  other  "User_Library-1210(3225M)_Cap_991:1"
  other  "User_Library-1210(3225M)_Cap_991:2"
  other  "User_Library-1210(3225M)_Cap_991:3"
  other  "User_Library-0201(0603M)_Cap_993:1"
  other  "User_Library-0201(0603M)_Cap_993:2"
  other  "User_Library-0201(0603M)_Cap_993:3"
  other  "User_Library-0805_SMD_Capacitor_995:1"
  other  "User_Library-0603(1608M)_Cap_997:1"
  other  "User_Library-0603(1608M)_Cap_997:2"
  other  "User_Library-0603(1608M)_Cap_997:3"
  other  "User_Library-0201(0603M)_Cap_999:1"
  other  "User_Library-0201(0603M)_Cap_999:2"
  other  "User_Library-0201(0603M)_Cap_999:3"
  other  "User_Library-0603(1608M)_Cap_1001:1"
  other  "User_Library-0603(1608M)_Cap_1001:2"
  other  "User_Library-0603(1608M)_Cap_1001:3"
  other  "User_Library-0603(1608M)_Cap_1003:1"
  other  "User_Library-0603(1608M)_Cap_1003:2"
  other  "User_Library-0603(1608M)_Cap_1003:3"
  other  "User_Library-0201(0603M)_Cap_1005:1"
  other  "User_Library-0201(0603M)_Cap_1005:2"
  other  "User_Library-0201(0603M)_Cap_1005:3"
  other  "User_Library-0201(0603M)_Cap_1007:1"
  other  "User_Library-0201(0603M)_Cap_1007:2"
  other  "User_Library-0201(0603M)_Cap_1007:3"
  other  "User_Library-0805_SMD_Capacitor_1009:1"
  other  "User_Library-1210(3225M)_Cap_1011:1"
  other  "User_Library-1210(3225M)_Cap_1011:2"
  other  "User_Library-1210(3225M)_Cap_1011:3"
  other  "User_Library-0201(0603M)_Cap_1013:1"
  other  "User_Library-0201(0603M)_Cap_1013:2"
  other  "User_Library-0201(0603M)_Cap_1013:3"
  other  "User_Library-0201(0603M)_Cap_1015:1"
  other  "User_Library-0201(0603M)_Cap_1015:2"
  other  "User_Library-0201(0603M)_Cap_1015:3"
  other  "User_Library-0201(0603M)_Cap_1017:1"
  other  "User_Library-0201(0603M)_Cap_1017:2"
  other  "User_Library-0201(0603M)_Cap_1017:3"
  other  "User_Library-0201(0603M)_Cap_1019:1"
  other  "User_Library-0201(0603M)_Cap_1019:2"
  other  "User_Library-0201(0603M)_Cap_1019:3"
  other  "User_Library-0603(1608M)_Cap_1021:1"
  other  "User_Library-0603(1608M)_Cap_1021:2"
  other  "User_Library-0603(1608M)_Cap_1021:3"
  other  "User_Library-0201(0603M)_Cap_1023:1"
  other  "User_Library-0201(0603M)_Cap_1023:2"
  other  "User_Library-0201(0603M)_Cap_1023:3"
  other  "User_Library-0201(0603M)_Cap_1025:1"
  other  "User_Library-0201(0603M)_Cap_1025:2"
  other  "User_Library-0201(0603M)_Cap_1025:3"
  other  "User_Library-0603(1608M)_Cap_1027:1"
  other  "User_Library-0603(1608M)_Cap_1027:2"
  other  "User_Library-0603(1608M)_Cap_1027:3"
  other  "User_Library-1210(3225M)_Cap_1029:1"
  other  "User_Library-1210(3225M)_Cap_1029:2"
  other  "User_Library-1210(3225M)_Cap_1029:3"
  other  "User_Library-0201(0603M)_Cap_1031:1"
  other  "User_Library-0201(0603M)_Cap_1031:2"
  other  "User_Library-0201(0603M)_Cap_1031:3"
  other  "User_Library-0201(0603M)_Cap_1033:1"
  other  "User_Library-0201(0603M)_Cap_1033:2"
  other  "User_Library-0201(0603M)_Cap_1033:3"
  other  "User_Library-0201(0603M)_Cap_1035:1"
  other  "User_Library-0201(0603M)_Cap_1035:2"
  other  "User_Library-0201(0603M)_Cap_1035:3"
  other  "User_Library-0201(0603M)_Cap_1037:1"
  other  "User_Library-0201(0603M)_Cap_1037:2"
  other  "User_Library-0201(0603M)_Cap_1037:3"
  other  "User_Library-0603(1608M)_Cap_1039:1"
  other  "User_Library-0603(1608M)_Cap_1039:2"
  other  "User_Library-0603(1608M)_Cap_1039:3"
  other  "User_Library-1210(3225M)_Cap_1041:1"
  other  "User_Library-1210(3225M)_Cap_1041:2"
  other  "User_Library-1210(3225M)_Cap_1041:3"
  other  "User_Library-0201(0603M)_Cap_1043:1"
  other  "User_Library-0201(0603M)_Cap_1043:2"
  other  "User_Library-0201(0603M)_Cap_1043:3"
  other  "User_Library-0201(0603M)_Cap_1045:1"
  other  "User_Library-0201(0603M)_Cap_1045:2"
  other  "User_Library-0201(0603M)_Cap_1045:3"
  other  "User_Library-0201(0603M)_Cap_1047:1"
  other  "User_Library-0201(0603M)_Cap_1047:2"
  other  "User_Library-0201(0603M)_Cap_1047:3"
  other  "User_Library-0201(0603M)_Cap_1049:1"
  other  "User_Library-0201(0603M)_Cap_1049:2"
  other  "User_Library-0201(0603M)_Cap_1049:3"
  other  "User_Library-0805_SMD_Capacitor_1051:1"
  other  "User_Library-0201(0603M)_Cap_1053:1"
  other  "User_Library-0201(0603M)_Cap_1053:2"
  other  "User_Library-0201(0603M)_Cap_1053:3"
  other  "User_Library-0603(1608M)_Cap_1055:1"
  other  "User_Library-0603(1608M)_Cap_1055:2"
  other  "User_Library-0603(1608M)_Cap_1055:3"
  other  "User_Library-0603(1608M)_Cap_1057:1"
  other  "User_Library-0603(1608M)_Cap_1057:2"
  other  "User_Library-0603(1608M)_Cap_1057:3"
  other  "User_Library-0201(0603M)_Cap_1059:1"
  other  "User_Library-0201(0603M)_Cap_1059:2"
  other  "User_Library-0201(0603M)_Cap_1059:3"
  other  "User_Library-0201(0603M)_Cap_1061:1"
  other  "User_Library-0201(0603M)_Cap_1061:2"
  other  "User_Library-0201(0603M)_Cap_1061:3"
  other  "User_Library-0603(1608M)_Cap_1063:1"
  other  "User_Library-0603(1608M)_Cap_1063:2"
  other  "User_Library-0603(1608M)_Cap_1063:3"
  other  "User_Library-0201(0603M)_Cap_1065:1"
  other  "User_Library-0201(0603M)_Cap_1065:2"
  other  "User_Library-0201(0603M)_Cap_1065:3"
  other  "User_Library-0201(0603M)_Cap_1067:1"
  other  "User_Library-0201(0603M)_Cap_1067:2"
  other  "User_Library-0201(0603M)_Cap_1067:3"
  other  "User_Library-0201(0603M)_Cap_1069:1"
  other  "User_Library-0201(0603M)_Cap_1069:2"
  other  "User_Library-0201(0603M)_Cap_1069:3"
  other  "User_Library-0201(0603M)_Cap_1071:1"
  other  "User_Library-0201(0603M)_Cap_1071:2"
  other  "User_Library-0201(0603M)_Cap_1071:3"
  other  "User_Library-0201(0603M)_Cap_1073:1"
  other  "User_Library-0201(0603M)_Cap_1073:2"
  other  "User_Library-0201(0603M)_Cap_1073:3"
  other  "User_Library-0201(0603M)_Cap_1075:1"
  other  "User_Library-0201(0603M)_Cap_1075:2"
  other  "User_Library-0201(0603M)_Cap_1075:3"
  other  "User_Library-0201(0603M)_Cap_1077:1"
  other  "User_Library-0201(0603M)_Cap_1077:2"
  other  "User_Library-0201(0603M)_Cap_1077:3"
  other  "User_Library-0201(0603M)_Cap_1079:1"
  other  "User_Library-0201(0603M)_Cap_1079:2"
  other  "User_Library-0201(0603M)_Cap_1079:3"
  other  "User_Library-0201(0603M)_Cap_1081:1"
  other  "User_Library-0201(0603M)_Cap_1081:2"
  other  "User_Library-0201(0603M)_Cap_1081:3"
  other  "User_Library-0201(0603M)_Cap_1083:1"
  other  "User_Library-0201(0603M)_Cap_1083:2"
  other  "User_Library-0201(0603M)_Cap_1083:3"
  other  "User_Library-0201(0603M)_Cap_1085:1"
  other  "User_Library-0201(0603M)_Cap_1085:2"
  other  "User_Library-0201(0603M)_Cap_1085:3"
  other  "User_Library-0201(0603M)_Cap_1087:1"
  other  "User_Library-0201(0603M)_Cap_1087:2"
  other  "User_Library-0201(0603M)_Cap_1087:3"
  other  "User_Library-0603(1608M)_Cap_1089:1"
  other  "User_Library-0603(1608M)_Cap_1089:2"
  other  "User_Library-0603(1608M)_Cap_1089:3"
  other  "User_Library-0603(1608M)_Cap_1091:1"
  other  "User_Library-0603(1608M)_Cap_1091:2"
  other  "User_Library-0603(1608M)_Cap_1091:3"
  other  "User_Library-0201(0603M)_Cap_1093:1"
  other  "User_Library-0201(0603M)_Cap_1093:2"
  other  "User_Library-0201(0603M)_Cap_1093:3"
  other  "User_Library-0201(0603M)_Cap_1095:1"
  other  "User_Library-0201(0603M)_Cap_1095:2"
  other  "User_Library-0201(0603M)_Cap_1095:3"
  other  "User_Library-0201(0603M)_Cap_1097:1"
  other  "User_Library-0201(0603M)_Cap_1097:2"
  other  "User_Library-0201(0603M)_Cap_1097:3"
  other  "User_Library-0201(0603M)_Cap_1099:1"
  other  "User_Library-0201(0603M)_Cap_1099:2"
  other  "User_Library-0201(0603M)_Cap_1099:3"
  other  "User_Library-0201(0603M)_Cap_1101:1"
  other  "User_Library-0201(0603M)_Cap_1101:2"
  other  "User_Library-0201(0603M)_Cap_1101:3"
  other  "User_Library-0201(0603M)_Cap_1103:1"
  other  "User_Library-0201(0603M)_Cap_1103:2"
  other  "User_Library-0201(0603M)_Cap_1103:3"
  other  "User_Library-0201(0603M)_Cap_1105:1"
  other  "User_Library-0201(0603M)_Cap_1105:2"
  other  "User_Library-0201(0603M)_Cap_1105:3"
  other  "User_Library-0201(0603M)_Cap_1107:1"
  other  "User_Library-0201(0603M)_Cap_1107:2"
  other  "User_Library-0201(0603M)_Cap_1107:3"
  other  "User_Library-0201(0603M)_Cap_1109:1"
  other  "User_Library-0201(0603M)_Cap_1109:2"
  other  "User_Library-0201(0603M)_Cap_1109:3"
  other  "User_Library-0201(0603M)_Cap_1111:1"
  other  "User_Library-0201(0603M)_Cap_1111:2"
  other  "User_Library-0201(0603M)_Cap_1111:3"
  other  "User_Library-0201(0603M)_Cap_1113:1"
  other  "User_Library-0201(0603M)_Cap_1113:2"
  other  "User_Library-0201(0603M)_Cap_1113:3"
  other  "User_Library-0402(1005M)_Cap_1115:1"
  other  "User_Library-0402(1005M)_Cap_1115:2"
  other  "User_Library-0402(1005M)_Cap_1115:3"
  other  "User_Library-0201(0603M)_Cap_1117:1"
  other  "User_Library-0201(0603M)_Cap_1117:2"
  other  "User_Library-0201(0603M)_Cap_1117:3"
  other  "User_Library-0201(0603M)_Cap_1119:1"
  other  "User_Library-0201(0603M)_Cap_1119:2"
  other  "User_Library-0201(0603M)_Cap_1119:3"
  other  "User_Library-0402(1005M)_Cap_1121:1"
  other  "User_Library-0402(1005M)_Cap_1121:2"
  other  "User_Library-0402(1005M)_Cap_1121:3"
  other  "User_Library-0201(0603M)_Cap_1123:1"
  other  "User_Library-0201(0603M)_Cap_1123:2"
  other  "User_Library-0201(0603M)_Cap_1123:3"
  other  "User_Library-0201(0603M)_Cap_1125:1"
  other  "User_Library-0201(0603M)_Cap_1125:2"
  other  "User_Library-0201(0603M)_Cap_1125:3"
  other  "User_Library-0201(0603M)_Cap_1127:1"
  other  "User_Library-0201(0603M)_Cap_1127:2"
  other  "User_Library-0201(0603M)_Cap_1127:3"
  other  "User_Library-0201(0603M)_Cap_1129:1"
  other  "User_Library-0201(0603M)_Cap_1129:2"
  other  "User_Library-0201(0603M)_Cap_1129:3"
  other  "User_Library-0201(0603M)_Cap_1131:1"
  other  "User_Library-0201(0603M)_Cap_1131:2"
  other  "User_Library-0201(0603M)_Cap_1131:3"
  other  "User_Library-0201(0603M)_Cap_1133:1"
  other  "User_Library-0201(0603M)_Cap_1133:2"
  other  "User_Library-0201(0603M)_Cap_1133:3"
  other  "User_Library-0201(0603M)_Cap_1135:1"
  other  "User_Library-0201(0603M)_Cap_1135:2"
  other  "User_Library-0201(0603M)_Cap_1135:3"
  other  "User_Library-0402(1005M)_Cap_1137:1"
  other  "User_Library-0402(1005M)_Cap_1137:2"
  other  "User_Library-0402(1005M)_Cap_1137:3"
  other  "User_Library-0201(0603M)_Cap_1139:1"
  other  "User_Library-0201(0603M)_Cap_1139:2"
  other  "User_Library-0201(0603M)_Cap_1139:3"
  other  "User_Library-0603(1608M)_Cap_1141:1"
  other  "User_Library-0603(1608M)_Cap_1141:2"
  other  "User_Library-0603(1608M)_Cap_1141:3"
  other  "User_Library-0201(0603M)_Cap_1143:1"
  other  "User_Library-0201(0603M)_Cap_1143:2"
  other  "User_Library-0201(0603M)_Cap_1143:3"
  other  "User_Library-0201(0603M)_Cap_1145:1"
  other  "User_Library-0201(0603M)_Cap_1145:2"
  other  "User_Library-0201(0603M)_Cap_1145:3"
  other  "User_Library-0201(0603M)_Cap_1147:1"
  other  "User_Library-0201(0603M)_Cap_1147:2"
  other  "User_Library-0201(0603M)_Cap_1147:3"
  other  "User_Library-0201(0603M)_Cap_1149:1"
  other  "User_Library-0201(0603M)_Cap_1149:2"
  other  "User_Library-0201(0603M)_Cap_1149:3"
  other  "User_Library-0402(1005M)_Cap_1151:1"
  other  "User_Library-0402(1005M)_Cap_1151:2"
  other  "User_Library-0402(1005M)_Cap_1151:3"
  other  "User_Library-0201(0603M)_Cap_1153:1"
  other  "User_Library-0201(0603M)_Cap_1153:2"
  other  "User_Library-0201(0603M)_Cap_1153:3"
  other  "User_Library-0201(0603M)_Cap_1155:1"
  other  "User_Library-0201(0603M)_Cap_1155:2"
  other  "User_Library-0201(0603M)_Cap_1155:3"
  other  "User_Library-0201(0603M)_Cap_1157:1"
  other  "User_Library-0201(0603M)_Cap_1157:2"
  other  "User_Library-0201(0603M)_Cap_1157:3"
  other  "User_Library-0201(0603M)_Cap_1159:1"
  other  "User_Library-0201(0603M)_Cap_1159:2"
  other  "User_Library-0201(0603M)_Cap_1159:3"
  other  "User_Library-0201(0603M)_Cap_1161:1"
  other  "User_Library-0201(0603M)_Cap_1161:2"
  other  "User_Library-0201(0603M)_Cap_1161:3"
  other  "User_Library-0201(0603M)_Cap_1163:1"
  other  "User_Library-0201(0603M)_Cap_1163:2"
  other  "User_Library-0201(0603M)_Cap_1163:3"
  other  "User_Library-0201(0603M)_Cap_1165:1"
  other  "User_Library-0201(0603M)_Cap_1165:2"
  other  "User_Library-0201(0603M)_Cap_1165:3"
  other  "User_Library-0201(0603M)_Cap_1167:1"
  other  "User_Library-0201(0603M)_Cap_1167:2"
  other  "User_Library-0201(0603M)_Cap_1167:3"
  other  "User_Library-0201(0603M)_Cap_1169:1"
  other  "User_Library-0201(0603M)_Cap_1169:2"
  other  "User_Library-0201(0603M)_Cap_1169:3"
  other  "User_Library-0201(0603M)_Cap_1171:1"
  other  "User_Library-0201(0603M)_Cap_1171:2"
  other  "User_Library-0201(0603M)_Cap_1171:3"
  other  "User_Library-0402(1005M)_Cap_1173:1"
  other  "User_Library-0402(1005M)_Cap_1173:2"
  other  "User_Library-0402(1005M)_Cap_1173:3"
  other  "User_Library-0201(0603M)_Cap_1175:1"
  other  "User_Library-0201(0603M)_Cap_1175:2"
  other  "User_Library-0201(0603M)_Cap_1175:3"
  other  "User_Library-0201(0603M)_Cap_1177:1"
  other  "User_Library-0201(0603M)_Cap_1177:2"
  other  "User_Library-0201(0603M)_Cap_1177:3"
  other  "User_Library-0201(0603M)_Cap_1179:1"
  other  "User_Library-0201(0603M)_Cap_1179:2"
  other  "User_Library-0201(0603M)_Cap_1179:3"
  other  "User_Library-0201(0603M)_Cap_1181:1"
  other  "User_Library-0201(0603M)_Cap_1181:2"
  other  "User_Library-0201(0603M)_Cap_1181:3"
  other  "User_Library-0201(0603M)_Cap_1183:1"
  other  "User_Library-0201(0603M)_Cap_1183:2"
  other  "User_Library-0201(0603M)_Cap_1183:3"
  other  "User_Library-0201(0603M)_Cap_1185:1"
  other  "User_Library-0201(0603M)_Cap_1185:2"
  other  "User_Library-0201(0603M)_Cap_1185:3"
  other  "User_Library-0201(0603M)_Cap_1187:1"
  other  "User_Library-0201(0603M)_Cap_1187:2"
  other  "User_Library-0201(0603M)_Cap_1187:3"
  other  "User_Library-0201(0603M)_Cap_1189:1"
  other  "User_Library-0201(0603M)_Cap_1189:2"
  other  "User_Library-0201(0603M)_Cap_1189:3"
  other  "User_Library-0201(0603M)_Cap_1191:1"
  other  "User_Library-0201(0603M)_Cap_1191:2"
  other  "User_Library-0201(0603M)_Cap_1191:3"
  other  "User_Library-0201(0603M)_Cap_1193:1"
  other  "User_Library-0201(0603M)_Cap_1193:2"
  other  "User_Library-0201(0603M)_Cap_1193:3"
  other  "User_Library-0201(0603M)_Cap_1195:1"
  other  "User_Library-0201(0603M)_Cap_1195:2"
  other  "User_Library-0201(0603M)_Cap_1195:3"
  other  "User_Library-0201(0603M)_Cap_1197:1"
  other  "User_Library-0201(0603M)_Cap_1197:2"
  other  "User_Library-0201(0603M)_Cap_1197:3"
  other  "User_Library-0201(0603M)_Cap_1199:1"
  other  "User_Library-0201(0603M)_Cap_1199:2"
  other  "User_Library-0201(0603M)_Cap_1199:3"
  other  "User_Library-0201(0603M)_Cap_1201:1"
  other  "User_Library-0201(0603M)_Cap_1201:2"
  other  "User_Library-0201(0603M)_Cap_1201:3"
  other  "User_Library-0201(0603M)_Cap_1203:1"
  other  "User_Library-0201(0603M)_Cap_1203:2"
  other  "User_Library-0201(0603M)_Cap_1203:3"
  other  "User_Library-0201(0603M)_Cap_1205:1"
  other  "User_Library-0201(0603M)_Cap_1205:2"
  other  "User_Library-0201(0603M)_Cap_1205:3"
  other  "User_Library-0201(0603M)_Cap_1207:1"
  other  "User_Library-0201(0603M)_Cap_1207:2"
  other  "User_Library-0201(0603M)_Cap_1207:3"
  other  "User_Library-0201(0603M)_Cap_1209:1"
  other  "User_Library-0201(0603M)_Cap_1209:2"
  other  "User_Library-0201(0603M)_Cap_1209:3"
  other  "User_Library-0201(0603M)_Cap_1211:1"
  other  "User_Library-0201(0603M)_Cap_1211:2"
  other  "User_Library-0201(0603M)_Cap_1211:3"
  other  "User_Library-0201(0603M)_Cap_1213:1"
  other  "User_Library-0201(0603M)_Cap_1213:2"
  other  "User_Library-0201(0603M)_Cap_1213:3"
  other  "User_Library-0201(0603M)_Cap_1215:1"
  other  "User_Library-0201(0603M)_Cap_1215:2"
  other  "User_Library-0201(0603M)_Cap_1215:3"
  other  "User_Library-0201(0603M)_Cap_1217:1"
  other  "User_Library-0201(0603M)_Cap_1217:2"
  other  "User_Library-0201(0603M)_Cap_1217:3"
  other  "User_Library-0201(0603M)_Cap_1219:1"
  other  "User_Library-0201(0603M)_Cap_1219:2"
  other  "User_Library-0201(0603M)_Cap_1219:3"
  other  "User_Library-0201(0603M)_Cap_1221:1"
  other  "User_Library-0201(0603M)_Cap_1221:2"
  other  "User_Library-0201(0603M)_Cap_1221:3"
  other  "User_Library-0201(0603M)_Cap_1223:1"
  other  "User_Library-0201(0603M)_Cap_1223:2"
  other  "User_Library-0201(0603M)_Cap_1223:3"
  other  "User_Library-0603(1608M)_Cap_1225:1"
  other  "User_Library-0603(1608M)_Cap_1225:2"
  other  "User_Library-0603(1608M)_Cap_1225:3"
  other  "User_Library-0201(0603M)_Cap_1227:1"
  other  "User_Library-0201(0603M)_Cap_1227:2"
  other  "User_Library-0201(0603M)_Cap_1227:3"
  other  "User_Library-0201(0603M)_Cap_1229:1"
  other  "User_Library-0201(0603M)_Cap_1229:2"
  other  "User_Library-0201(0603M)_Cap_1229:3"
  other  "User_Library-0201(0603M)_Cap_1231:1"
  other  "User_Library-0201(0603M)_Cap_1231:2"
  other  "User_Library-0201(0603M)_Cap_1231:3"
  other  "User_Library-0201(0603M)_Cap_1233:1"
  other  "User_Library-0201(0603M)_Cap_1233:2"
  other  "User_Library-0201(0603M)_Cap_1233:3"
  extrude  "Extruded_1235:1"  [1 undecoded]
  other  "c-2129320-3-b-3d_1238:1"
  other  "c-5177983-2-a-3d_1240:1"
  other  "KMMX-AB10-SMT1SB30TR_rA1_1242:1"
  extrude  "Extruded_1244:1"  [1 undecoded]
  extrude  "Extruded_1247:1"  [1 undecoded]
  other  "WE-VS_0603_VS_1250:1"
  other  "User_Library-0201(0603M)_Cap_1252:1"
  other  "User_Library-0201(0603M)_Cap_1252:2"
  other  "User_Library-0201(0603M)_Cap_1252:3"
  extrude  "Extruded_1254:1"  [1 undecoded]
  extrude  "Extruded_1257:1"  [1 undecoded]
  other  "User_Library-0201(0603M)_Cap_1260:1"
  other  "User_Library-0201(0603M)_Cap_1260:2"
  other  "User_Library-0201(0603M)_Cap_1260:3"
  other  "User_Library-0201(0603M)_Cap_1262:1"
  other  "User_Library-0201(0603M)_Cap_1262:2"
  other  "User_Library-0201(0603M)_Cap_1262:3"
  other  "User_Library-0201(0603M)_Cap_1264:1"
  other  "User_Library-0201(0603M)_Cap_1264:2"
  other  "User_Library-0201(0603M)_Cap_1264:3"
  other  "User_Library-0201(0603M)_Cap_1266:1"
  other  "User_Library-0201(0603M)_Cap_1266:2"
  other  "User_Library-0201(0603M)_Cap_1266:3"
  other  "User_Library-0201(0603M)_Cap_1268:1"
  other  "User_Library-0201(0603M)_Cap_1268:2"
  other  "User_Library-0201(0603M)_Cap_1268:3"
  other  "User_Library-0201(0603M)_Cap_1270:1"
  other  "User_Library-0201(0603M)_Cap_1270:2"
  other  "User_Library-0201(0603M)_Cap_1270:3"
  other  "User_Library-0201(0603M)_Cap_1272:1"
  other  "User_Library-0201(0603M)_Cap_1272:2"
  other  "User_Library-0201(0603M)_Cap_1272:3"
  other  "User_Library-0201(0603M)_Cap_1274:1"
  other  "User_Library-0201(0603M)_Cap_1274:2"
  other  "User_Library-0201(0603M)_Cap_1274:3"
  other  "User_Library-0201(0603M)_Cap_1276:1"
  other  "User_Library-0201(0603M)_Cap_1276:2"
  other  "User_Library-0201(0603M)_Cap_1276:3"
  other  "User_Library-0201(0603M)_Cap_1278:1"
  other  "User_Library-0201(0603M)_Cap_1278:2"
  other  "User_Library-0201(0603M)_Cap_1278:3"
  other  "User_Library-0201(0603M)_Cap_1280:1"
  other  "User_Library-0201(0603M)_Cap_1280:2"
  other  "User_Library-0201(0603M)_Cap_1280:3"
  other  "User_Library-LTST-C190GKT_Pad005_725:7"
  other  "User_Library-LTST-C190GKT_Pad001_726:13"
  other  "User_Library-LTST-C190GKT_Pad001_726:14"
  other  "User_Library-LTST-C190GKT_Pad004_727:7"
  other  "User_Library-LTST-C190GKT_Pad003_728:13"
  other  "User_Library-LTST-C190GKT_Pad003_728:14"
  other  "User_Library-LTST-C190GKT_Lens_729:7"
  other  "User_Library-LTST-C190GKT_Pad_730:7"
  extrude  "Extruded_1284:1"  [1 undecoded]
  other  "Cylinder_1286:1"
  extrude  "Extruded_1284:2"  [1 undecoded]
  other  "Cylinder_1290:1"
  other  "Cylinder_1286:2"
  extrude  "Extruded_1284:3"  [1 undecoded]
  other  "RES-0201(0603mm)_1296:1"
  other  "RES-0201(0603mm)_1296:2"
  other  "RES-0201(0603mm)_1296:3"
  other  "RES-0201(0603mm)_1296:4"
  other  "RES-0201(0603mm)_1298:1"
  other  "RES-0201(0603mm)_1298:2"
  other  "RES-0201(0603mm)_1298:3"
  other  "RES-0201(0603mm)_1298:4"
  other  "RES-0201(0603mm)_1300:1"
  other  "RES-0201(0603mm)_1300:2"
  other  "RES-0201(0603mm)_1300:3"
  other  "RES-0201(0603mm)_1300:4"
  other  "RES-0201(0603mm)_1302:1"
  other  "RES-0201(0603mm)_1302:2"
  other  "RES-0201(0603mm)_1302:3"
  other  "RES-0201(0603mm)_1302:4"
  other  "RES-0201(0603mm)_1304:1"
  other  "RES-0201(0603mm)_1304:2"
  other  "RES-0201(0603mm)_1304:3"
  other  "RES-0201(0603mm)_1304:4"
  other  "RES-0201(0603mm)_1306:1"
  other  "RES-0201(0603mm)_1306:2"
  other  "RES-0201(0603mm)_1306:3"
  other  "RES-0201(0603mm)_1306:4"
  other  "RES-0201(0603mm)_1308:1"
  other  "RES-0201(0603mm)_1308:2"
  other  "RES-0201(0603mm)_1308:3"
  other  "RES-0201(0603mm)_1308:4"
  other  "RES-0201(0603mm)_1310:1"
  other  "RES-0201(0603mm)_1310:2"
  other  "RES-0201(0603mm)_1310:3"
  other  "RES-0201(0603mm)_1310:4"
  other  "RES-0201(0603mm)_1312:1"
  other  "RES-0201(0603mm)_1312:2"
  other  "RES-0201(0603mm)_1312:3"
  other  "RES-0201(0603mm)_1312:4"
  extrude  "Extruded_1314:1"  [1 undecoded]
  other  "User_Library-SOT-23-3-1_SOT-23-3_Body_639:7"
  other  "User_Library-SOT-23-3-1_SOT-23-3_Foot_640:7"
  other  "User_Library-SOT-23-3-1_SOT-23-3_Foot_641:7"
  other  "User_Library-SOT-23-3-1_SOT-23-3_Foot_642:7"
  other  "RES-0201(0603mm)_1319:1"
  other  "RES-0201(0603mm)_1319:2"
  other  "RES-0201(0603mm)_1319:3"
  other  "RES-0201(0603mm)_1319:4"
  other  "RES-0201(0603mm)_1321:1"
  other  "RES-0201(0603mm)_1321:2"
  other  "RES-0201(0603mm)_1321:3"
  other  "RES-0201(0603mm)_1321:4"
  other  "Composite1"
  other  "Srf1"
note: 30 required parameter values undecoded (feature->parameter linkage not recoverable at this tier; creation-order binding heuristic only, values carry confidence <= 0.55)
